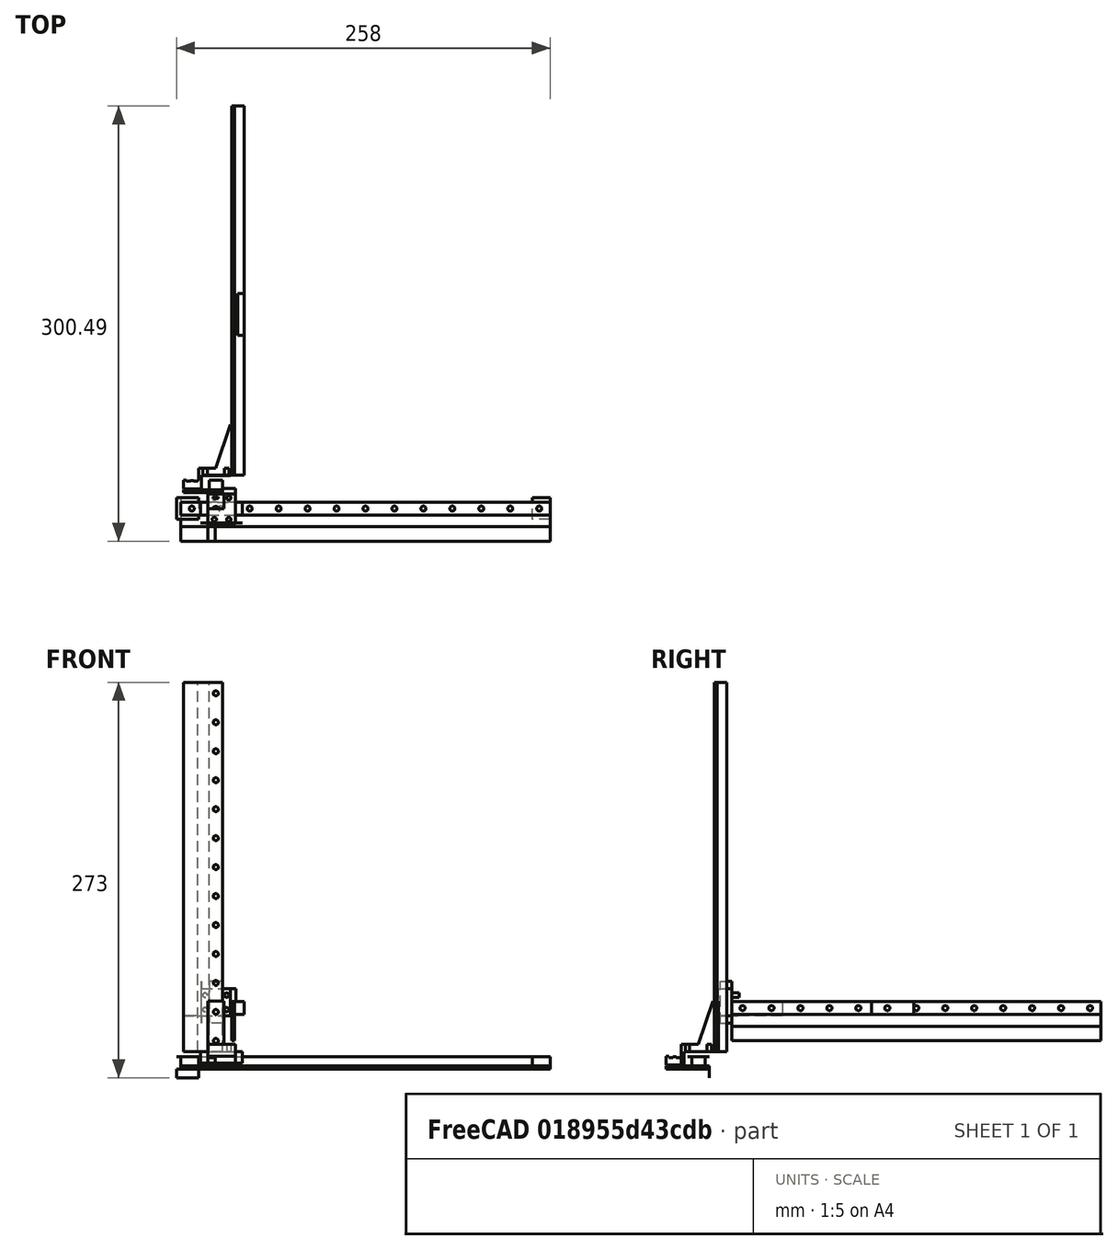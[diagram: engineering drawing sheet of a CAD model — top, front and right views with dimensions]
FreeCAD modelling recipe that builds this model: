
FCSTD DOCUMENT  (FreeCAD 0.21R33668 +26 (Git))
Label: v7
License: All rights reserved
LicenseURL: http://en.wikipedia.org/wiki/All_rights_reserved
objects: App::FeaturePython×94, Part::FeaturePython×66, App::Link×14
note: 65 computed .brp shape members not serialized (recipe doc carries the construction recipe); baked Part::Feature solids carry a one-line shape summary decoded from their .brp
EXTERNAL_REF file=parts/Base.FCStd obj=Body
EXTERNAL_REF file=parts/PCB_Linear_Potentiometer.FCStd obj=Body
EXTERNAL_REF file=parts/MG/mgn9c_13.FCStd obj=Body
EXTERNAL_REF file=parts/MG/mgn9c_slide.FCStd obj=Body001
EXTERNAL_REF file=parts/NormalConnector.FCStd obj=Body
EXTERNAL_REF file=parts/Joystick_Holder.FCStd obj=Body

FEATURE [App::Link] Link  label="Base_PCBLB"
  LinkedObject = -> <external parts/Base.FCStd>#Body
  _LinkOwner = 433
FEATURE [App::Link] Link001  label="PCB"
  LinkPlacement = pos=(-2.497e-13,7.45963e-11,-2) rot=(0,0,1;0rad)
  LinkedObject = -> <external parts/PCB_Linear_Potentiometer.FCStd>#Body
  Placement = pos=(-2.497e-13,7.45963e-11,-2) rot=(0,0,1;0rad)
  _LinkOwner = 433
FEATURE [App::Link] Link002  label="RailXL"
  LinkPlacement = pos=(1.4e-15,8e-16,-3.48e-14) rot=(0,0,1;0rad)
  LinkedObject = -> <external parts/MG/mgn9c_13.FCStd>#Body
  Placement = pos=(1.4e-15,8e-16,-3.48e-14) rot=(0,0,1;0rad)
  _LinkOwner = 433
FEATURE [App::Link] Link003  label="Base_PCB"
  LinkPlacement = pos=(255,9,-4.15529e-11) rot=(0,0,1;3.14159rad)
  LinkedObject = -> <external parts/Base.FCStd>#Body
  Placement = pos=(255,9,-4.15529e-11) rot=(0,0,1;3.14159rad)
  _LinkOwner = 433
FEATURE [App::Link] Link004  label="Slide"
  LinkPlacement = pos=(13.624,-5.5,2) rot=(0,0,1;0rad)
  LinkedObject = -> <external parts/MG/mgn9c_slide.FCStd>#Body001
  Placement = pos=(13.624,-5.5,2) rot=(0,0,1;0rad)
  _LinkOwner = 433
FEATURE [App::Link] Link005  label="NormalConnector"
  LinkPlacement = pos=(18.624,-5.5,4.00003) rot=(0,0,1;0rad)
  LinkedObject = -> <external parts/NormalConnector.FCStd>#Body
  Placement = pos=(18.624,-5.5,4.00003) rot=(0,0,1;0rad)
  _LinkOwner = 433
FEATURE [App::Link] Link006  label="PCB001"
  LinkPlacement = pos=(19.624,15.5,10) rot=(0.57735,0.57735,0.57735;4.18879rad)
  LinkedObject = -> <external parts/PCB_Linear_Potentiometer.FCStd>#Body
  Placement = pos=(19.624,15.5,10) rot=(0.57735,0.57735,0.57735;4.18879rad)
  _LinkOwner = 433
FEATURE [App::Link] Link007  label="Rail"
  LinkPlacement = pos=(19.624,17.5,10) rot=(0.57735,0.57735,0.57735;4.18879rad)
  LinkedObject = -> <external parts/MG/mgn9c_13.FCStd>#Body
  Placement = pos=(19.624,17.5,10) rot=(0.57735,0.57735,0.57735;4.18879rad)
  _LinkOwner = 433
FEATURE [App::Link] Link008  label="Slide001"
  LinkPlacement = pos=(34.124,19.5,58.4856) rot=(-0.57735,0.57735,0.57735;2.0944rad)
  LinkedObject = -> <external parts/MG/mgn9c_slide.FCStd>#Body001
  Placement = pos=(34.124,19.5,58.4856) rot=(-0.57735,0.57735,0.57735;2.0944rad)
  _LinkOwner = 433
FEATURE [App::Link] Link009  label="NormalConnector001"
  LinkPlacement = pos=(14.124,21.5,34.5856) rot=(0.57735,0.57735,0.57735;4.18879rad)
  LinkedObject = -> <external parts/NormalConnector.FCStd>#Body
  Placement = pos=(14.124,21.5,34.5856) rot=(0.57735,0.57735,0.57735;4.18879rad)
  _LinkOwner = 433
FEATURE [App::Link] Link010  label="Rail001"
  LinkPlacement = pos=(37.124,27.5,35.5856) rot=(0.57735,0.57735,0.57735;2.0944rad)
  LinkedObject = -> <external parts/MG/mgn9c_13.FCStd>#Body
  Placement = pos=(37.124,27.5,35.5856) rot=(0.57735,0.57735,0.57735;2.0944rad)
  _LinkOwner = 433
FEATURE [App::Link] Link011  label="PCB002"
  LinkPlacement = pos=(35.124,27.5,35.5856) rot=(0.57735,0.57735,0.57735;2.0944rad)
  LinkedObject = -> <external parts/PCB_Linear_Potentiometer.FCStd>#Body
  Placement = pos=(35.124,27.5,35.5856) rot=(0.57735,0.57735,0.57735;2.0944rad)
  _LinkOwner = 433
FEATURE [App::Link] Link012  label="Slide002"
  LinkPlacement = pos=(39.124,153.145,50.0856) rot=(0.57735,-0.57735,0.57735;4.18879rad)
  LinkedObject = -> <external parts/MG/mgn9c_slide.FCStd>#Body001
  Placement = pos=(39.124,153.145,50.0856) rot=(0.57735,-0.57735,0.57735;4.18879rad)
  _LinkOwner = 433
FEATURE [App::Link] Link013  label="JoystickHolder"
  LinkPlacement = pos=(171.029,100,-4) rot=(0,0,1;3.14159rad)
  LinkedObject = -> <external parts/Joystick_Holder.FCStd>#Body
  Placement = pos=(171.029,100,-4) rot=(0,0,1;3.14159rad)
  _LinkOwner = 433
FEATURE [Part::FeaturePython] Parts  # WARN: FeaturePython — macro-defined, semantics opaque (R4)
  Group = -> [Link,Link001,Link002,Link003,Link004,Link005,Link006,Link007,Link008,Link009,Link010,Link011,Link012,Link013]
  GroupMode = 0
FEATURE [Part::FeaturePython] Assembly  # WARN: FeaturePython — macro-defined, semantics opaque (R4)
  AutoRelax = true
  BuildShape = 0
  Freeze = false
  Group = -> [Constraints,Elements,Parts]
  Verbose = false
  _SolverType = 1
  _Version = 1
FEATURE [App::FeaturePython] Constraints  # WARN: FeaturePython — macro-defined, semantics opaque (R4)
  Group = -> [Constraint,Constraint001,Constraint003,Constraint004,Constraint005,Constraint006,Constraint007,Constraint008,Constraint009,Constraint010,Constraint011,Constraint012,Constraint019,Constraint020,Constraint021,Constraint022,Constraint023,Constraint025,Constraint026,Constraint027,Constraint029,Constraint030,Constraint031,Constraint035,Constraint037,Constraint038,Constraint039,Constraint040,+3 more]
  _Version = 1
FEATURE [App::FeaturePython] Elements  # WARN: FeaturePython — macro-defined, semantics opaque (R4)
  Group = -> [_Element,_Element001,_Element002,_Element003,_Element004,_Element005,_Element006,_Element007,_Element008,_Element009,_Element010,_Element011,_Element012,_Element013,_Element014,_Element015,_Element016,_Element017,_Element018,_Element019,_Element020,_Element021,_Element022,_Element023,_Element024,_Element025,_Element026,_Element027,_Element028,_Element029,_Element030,_Element031,_Element032,+31 more]
FEATURE [App::FeaturePython] Constraint  label="Locked"  # WARN: FeaturePython — macro-defined, semantics opaque (R4)
  Disabled = false
  Group = -> [ElementLink]
  _ConstraintType = 0
  _Parent = -> Constraints
FEATURE [App::FeaturePython] ElementLink  label="_Element"  # link proxy (typed FeaturePython)
  LinkTransform = true
  LinkedObject = -> _Element
  _Parent = -> Constraint
FEATURE [Part::FeaturePython] _Element  # link proxy (typed FeaturePython)
  Detach = false
  LinkTransform = true
  LinkedObject = -> Link [Pocket.Face5]
  _Parent = -> Elements
FEATURE [App::FeaturePython] Constraint001  label="PlaneAlignment"  # WARN: FeaturePython — macro-defined, semantics opaque (R4)
  Angle = 0
  AnglePitch = 0
  AngleRoll = 0
  Cascade = false
  Disabled = false
  Group = -> [ElementLink001,ElementLink002]
  LockAngle = false
  _ConstraintType = 37
  _Parent = -> Constraints
FEATURE [App::FeaturePython] ElementLink001  label="_Element001"  # link proxy (typed FeaturePython)
  LinkTransform = true
  LinkedObject = -> _Element001
  _Parent = -> Constraint001
FEATURE [Part::FeaturePython] _Element001  # link proxy (typed FeaturePython)
  Detach = false
  LinkTransform = true
  LinkedObject = -> Link001 [Pad001.Face4]
  _Parent = -> Elements
FEATURE [App::FeaturePython] ElementLink002  label="_Element002"  # link proxy (typed FeaturePython)
  LinkTransform = true
  LinkedObject = -> _Element002
  _Parent = -> Constraint001
FEATURE [Part::FeaturePython] _Element002  # link proxy (typed FeaturePython)
  Detach = false
  LinkTransform = true
  LinkedObject = -> Link [Pocket.Face11]
  _Parent = -> Elements
FEATURE [Part::FeaturePython] _Element003  # link proxy (typed FeaturePython)
  Detach = false
  LinkTransform = true
  LinkedObject = -> Link [Pocket.Face18]
  _Parent = -> Elements
FEATURE [Part::FeaturePython] _Element004  # link proxy (typed FeaturePython)
  Detach = false
  LinkTransform = true
  LinkedObject = -> Link001 [Pad001.Face1]
  _Parent = -> Elements
FEATURE [App::FeaturePython] Constraint003  label="PlaneAlignment002"  # WARN: FeaturePython — macro-defined, semantics opaque (R4)
  Angle = 0
  AnglePitch = 0
  AngleRoll = 0
  Cascade = false
  Disabled = false
  Group = -> [ElementLink005,ElementLink006]
  LockAngle = false
  _ConstraintType = 37
  _Parent = -> Constraints
FEATURE [App::FeaturePython] ElementLink005  label="_Element005"  # link proxy (typed FeaturePython)
  LinkTransform = true
  LinkedObject = -> _Element005
  _Parent = -> Constraint003
FEATURE [Part::FeaturePython] _Element005  # link proxy (typed FeaturePython)
  Detach = false
  LinkTransform = true
  LinkedObject = -> Link001 [Pad001.Face2]
  _Parent = -> Elements
FEATURE [App::FeaturePython] ElementLink006  label="_Element006"  # link proxy (typed FeaturePython)
  LinkTransform = true
  LinkedObject = -> _Element006
  _Parent = -> Constraint003
FEATURE [Part::FeaturePython] _Element006  # link proxy (typed FeaturePython)
  Detach = false
  LinkTransform = true
  LinkedObject = -> Link [Pocket.Face4]
  _Parent = -> Elements
FEATURE [App::FeaturePython] Constraint004  label="PlaneAlignment003"  # WARN: FeaturePython — macro-defined, semantics opaque (R4)
  Angle = 0
  AnglePitch = 0
  AngleRoll = 0
  Cascade = false
  Disabled = false
  Group = -> [ElementLink007,ElementLink008]
  LockAngle = false
  _ConstraintType = 37
  _Parent = -> Constraints
FEATURE [App::FeaturePython] ElementLink007  label="_Element007"  # link proxy (typed FeaturePython)
  LinkTransform = true
  LinkedObject = -> _Element007
  _Parent = -> Constraint004
FEATURE [Part::FeaturePython] _Element007  # link proxy (typed FeaturePython)
  Detach = false
  LinkTransform = true
  LinkedObject = -> Link [Pocket.Face1]
  _Parent = -> Elements
FEATURE [App::FeaturePython] ElementLink008  label="_Element008"  # link proxy (typed FeaturePython)
  LinkTransform = true
  LinkedObject = -> _Element008
  _Parent = -> Constraint004
FEATURE [Part::FeaturePython] _Element008  # link proxy (typed FeaturePython)
  Detach = false
  LinkTransform = true
  LinkedObject = -> Link002 [LinearPattern.Face2]
  _Parent = -> Elements
FEATURE [App::FeaturePython] Constraint005  label="PlaneAlignment004"  # WARN: FeaturePython — macro-defined, semantics opaque (R4)
  Angle = 0
  AnglePitch = 0
  AngleRoll = 0
  Cascade = false
  Disabled = false
  Group = -> [ElementLink009,ElementLink010]
  LockAngle = false
  _ConstraintType = 37
  _Parent = -> Constraints
FEATURE [App::FeaturePython] ElementLink009  label="_Element009"  # link proxy (typed FeaturePython)
  LinkTransform = true
  LinkedObject = -> _Element009
  _Parent = -> Constraint005
FEATURE [Part::FeaturePython] _Element009  # link proxy (typed FeaturePython)
  Detach = false
  LinkTransform = true
  LinkedObject = -> Link002 [LinearPattern.Face6]
  _Parent = -> Elements
FEATURE [App::FeaturePython] ElementLink010  label="_Element010"  # link proxy (typed FeaturePython)
  LinkTransform = true
  LinkedObject = -> _Element010
  _Parent = -> Constraint005
FEATURE [Part::FeaturePython] _Element010  # link proxy (typed FeaturePython)
  Detach = false
  LinkTransform = true
  LinkedObject = -> Link [Pocket.Face3]
  _Parent = -> Elements
FEATURE [App::FeaturePython] Constraint006  label="PlaneAlignment005"  # WARN: FeaturePython — macro-defined, semantics opaque (R4)
  Angle = 0
  AnglePitch = 0
  AngleRoll = 0
  Cascade = false
  Disabled = false
  Group = -> [ElementLink011,ElementLink012]
  LockAngle = false
  _ConstraintType = 37
  _Parent = -> Constraints
FEATURE [App::FeaturePython] ElementLink011  label="_Element011"  # link proxy (typed FeaturePython)
  LinkTransform = true
  LinkedObject = -> _Element011
  _Parent = -> Constraint006
FEATURE [Part::FeaturePython] _Element011  # link proxy (typed FeaturePython)
  Detach = false
  LinkTransform = true
  LinkedObject = -> Link002 [LinearPattern.Face4]
  _Parent = -> Elements
FEATURE [App::FeaturePython] ElementLink012  label="_Element012"  # link proxy (typed FeaturePython)
  LinkTransform = true
  LinkedObject = -> _Element012
  _Parent = -> Constraint006
FEATURE [Part::FeaturePython] _Element012  # link proxy (typed FeaturePython)
  Detach = false
  LinkTransform = true
  LinkedObject = -> Link001 [Pad001.Face5]
  _Parent = -> Elements
FEATURE [App::FeaturePython] Constraint007  label="PlaneAlignment006"  # WARN: FeaturePython — macro-defined, semantics opaque (R4)
  Angle = 0
  AnglePitch = 0
  AngleRoll = 0
  Cascade = false
  Disabled = false
  Group = -> [ElementLink013,ElementLink014]
  LockAngle = false
  _ConstraintType = 37
  _Parent = -> Constraints
FEATURE [App::FeaturePython] ElementLink013  label="_Element004"  # link proxy (typed FeaturePython)
  LinkTransform = true
  LinkedObject = -> _Element004
  _Parent = -> Constraint007
FEATURE [App::FeaturePython] ElementLink014  label="_Element009"  # link proxy (typed FeaturePython)
  LinkTransform = true
  LinkedObject = -> _Element009
  _Parent = -> Constraint007
FEATURE [App::FeaturePython] Constraint008  label="PlaneAlignment007"  # WARN: FeaturePython — macro-defined, semantics opaque (R4)
  Angle = 0
  AnglePitch = 0
  AngleRoll = 0
  Cascade = false
  Disabled = false
  Group = -> [ElementLink015,ElementLink016]
  LockAngle = false
  _ConstraintType = 37
  _Parent = -> Constraints
FEATURE [App::FeaturePython] ElementLink015  label="_Element013"  # link proxy (typed FeaturePython)
  LinkTransform = true
  LinkedObject = -> _Element013
  _Parent = -> Constraint008
FEATURE [Part::FeaturePython] _Element013  # link proxy (typed FeaturePython)
  Detach = false
  LinkTransform = true
  LinkedObject = -> Link003 [Pocket.Face2]
  _Parent = -> Elements
FEATURE [App::FeaturePython] ElementLink016  label="_Element009"  # link proxy (typed FeaturePython)
  LinkTransform = true
  LinkedObject = -> _Element009
  _Parent = -> Constraint008
FEATURE [App::FeaturePython] Constraint009  label="PlaneAlignment008"  # WARN: FeaturePython — macro-defined, semantics opaque (R4)
  Angle = 0
  AnglePitch = 0
  AngleRoll = 0
  Cascade = false
  Disabled = false
  Group = -> [ElementLink017,ElementLink018]
  LockAngle = false
  _ConstraintType = 37
  _Parent = -> Constraints
FEATURE [App::FeaturePython] ElementLink017  label="_Element014"  # link proxy (typed FeaturePython)
  LinkTransform = true
  LinkedObject = -> _Element014
  _Parent = -> Constraint009
FEATURE [Part::FeaturePython] _Element014  # link proxy (typed FeaturePython)
  Detach = false
  LinkTransform = true
  LinkedObject = -> Link003 [Pocket.Face11]
  _Parent = -> Elements
FEATURE [App::FeaturePython] ElementLink018  label="_Element001"  # link proxy (typed FeaturePython)
  LinkTransform = true
  LinkedObject = -> _Element001
  _Parent = -> Constraint009
FEATURE [App::FeaturePython] Constraint010  label="PlaneAlignment009"  # WARN: FeaturePython — macro-defined, semantics opaque (R4)
  Angle = 0
  AnglePitch = 0
  AngleRoll = 0
  Cascade = false
  Disabled = false
  Group = -> [ElementLink019,ElementLink020]
  LockAngle = false
  _ConstraintType = 37
  _Parent = -> Constraints
FEATURE [App::FeaturePython] ElementLink019  label="_Element015"  # link proxy (typed FeaturePython)
  LinkTransform = true
  LinkedObject = -> _Element015
  _Parent = -> Constraint010
FEATURE [Part::FeaturePython] _Element015  # link proxy (typed FeaturePython)
  Detach = false
  LinkTransform = true
  LinkedObject = -> Link003 [Pocket.Face1]
  _Parent = -> Elements
FEATURE [App::FeaturePython] ElementLink020  label="_Element016"  # link proxy (typed FeaturePython)
  LinkTransform = true
  LinkedObject = -> _Element016
  _Parent = -> Constraint010
FEATURE [Part::FeaturePython] _Element016  # link proxy (typed FeaturePython)
  Detach = false
  LinkTransform = true
  LinkedObject = -> Link002 [LinearPattern.Face3]
  _Parent = -> Elements
FEATURE [App::FeaturePython] Constraint011  label="PlaneAlignment010"  # WARN: FeaturePython — macro-defined, semantics opaque (R4)
  Angle = 0
  AnglePitch = 0
  AngleRoll = 0
  Cascade = false
  Disabled = false
  Group = -> [ElementLink021,ElementLink022]
  LockAngle = false
  _ConstraintType = 37
  _Parent = -> Constraints
FEATURE [App::FeaturePython] ElementLink021  label="_Element017"  # link proxy (typed FeaturePython)
  LinkTransform = true
  LinkedObject = -> _Element017
  _Parent = -> Constraint011
FEATURE [Part::FeaturePython] _Element017  # link proxy (typed FeaturePython)
  Detach = false
  LinkTransform = true
  LinkedObject = -> Link004 [Pocket003.Face12]
  _Parent = -> Elements
FEATURE [App::FeaturePython] ElementLink022  label="_Element009"  # link proxy (typed FeaturePython)
  LinkTransform = true
  LinkedObject = -> _Element009
  _Parent = -> Constraint011
FEATURE [App::FeaturePython] Constraint012  label="PlaneAlignment011"  # WARN: FeaturePython — macro-defined, semantics opaque (R4)
  Angle = 0
  AnglePitch = 0
  AngleRoll = 0
  Cascade = false
  Disabled = false
  Group = -> [ElementLink023,ElementLink024]
  LockAngle = false
  _ConstraintType = 37
  _Parent = -> Constraints
FEATURE [App::FeaturePython] ElementLink023  label="_Element018"  # link proxy (typed FeaturePython)
  LinkTransform = true
  LinkedObject = -> _Element018
  _Parent = -> Constraint012
FEATURE [Part::FeaturePython] _Element018  # link proxy (typed FeaturePython)
  Detach = false
  LinkTransform = true
  LinkedObject = -> Link004 [Pocket003.Face11]
  _Parent = -> Elements
FEATURE [App::FeaturePython] ElementLink024  label="_Element019"  # link proxy (typed FeaturePython)
  LinkTransform = true
  LinkedObject = -> _Element019
  _Parent = -> Constraint012
FEATURE [Part::FeaturePython] _Element019  # link proxy (typed FeaturePython)
  Detach = false
  LinkTransform = true
  LinkedObject = -> Link002 [LinearPattern.Face5]
  _Parent = -> Elements
FEATURE [Part::FeaturePython] _Element020  # link proxy (typed FeaturePython)
  Detach = false
  LinkTransform = true
  LinkedObject = -> Link005 [Pocket006.Face5]
  _Parent = -> Elements
FEATURE [Part::FeaturePython] _Element021  # link proxy (typed FeaturePython)
  Detach = false
  LinkTransform = true
  LinkedObject = -> Link004 [Pocket003.Face5]
  _Parent = -> Elements
FEATURE [Part::FeaturePython] _Element022  # link proxy (typed FeaturePython)
  Detach = false
  LinkTransform = true
  LinkedObject = -> Link005 [Pocket006.Face2]
  _Parent = -> Elements
FEATURE [Part::FeaturePython] _Element023  # link proxy (typed FeaturePython)
  Detach = false
  LinkTransform = true
  LinkedObject = -> Link004 [Pocket003.Face6]
  _Parent = -> Elements
FEATURE [Part::FeaturePython] _Element024  # link proxy (typed FeaturePython)
  Detach = false
  LinkTransform = true
  LinkedObject = -> Link005 [Pocket006.Face1]
  _Parent = -> Elements
FEATURE [Part::FeaturePython] _Element025  # link proxy (typed FeaturePython)
  Detach = false
  LinkTransform = true
  LinkedObject = -> Link004 [Pocket003.Face1]
  _Parent = -> Elements
FEATURE [Part::FeaturePython] _Element026  # link proxy (typed FeaturePython)
  Detach = false
  LinkTransform = true
  LinkedObject = -> Link006 [Pad001.Face1]
  _Parent = -> Elements
FEATURE [Part::FeaturePython] _Element027  # link proxy (typed FeaturePython)
  Detach = false
  LinkTransform = true
  LinkedObject = -> Link005 [Pocket006.Face9]
  _Parent = -> Elements
FEATURE [Part::FeaturePython] _Element028  # link proxy (typed FeaturePython)
  Detach = false
  LinkTransform = true
  LinkedObject = -> Link006 [Pad001.Face4]
  _Parent = -> Elements
FEATURE [Part::FeaturePython] _Element029  # link proxy (typed FeaturePython)
  Detach = false
  LinkTransform = true
  LinkedObject = -> Link005 [Pocket006.Face7]
  _Parent = -> Elements
FEATURE [Part::FeaturePython] _Element030  # link proxy (typed FeaturePython)
  Detach = false
  LinkTransform = true
  LinkedObject = -> Link006 [Pad001.Face2]
  _Parent = -> Elements
FEATURE [App::FeaturePython] Constraint019  label="PlaneAlignment018"  # WARN: FeaturePython — macro-defined, semantics opaque (R4)
  Angle = 0
  AnglePitch = 0
  AngleRoll = 0
  Cascade = false
  Disabled = false
  Group = -> [ElementLink037,ElementLink038]
  LockAngle = false
  _ConstraintType = 37
  _Parent = -> Constraints
FEATURE [App::FeaturePython] ElementLink037  label="_Element031"  # link proxy (typed FeaturePython)
  LinkTransform = true
  LinkedObject = -> _Element031
  _Parent = -> Constraint019
FEATURE [Part::FeaturePython] _Element031  # link proxy (typed FeaturePython)
  Detach = false
  LinkTransform = true
  LinkedObject = -> Link007 [LinearPattern.Face6]
  _Parent = -> Elements
FEATURE [App::FeaturePython] ElementLink038  label="_Element026"  # link proxy (typed FeaturePython)
  LinkTransform = true
  LinkedObject = -> _Element026
  _Parent = -> Constraint019
FEATURE [App::FeaturePython] Constraint020  label="PlaneAlignment019"  # WARN: FeaturePython — macro-defined, semantics opaque (R4)
  Angle = 0
  AnglePitch = 0
  AngleRoll = 0
  Cascade = false
  Disabled = false
  Group = -> [ElementLink039,ElementLink040]
  LockAngle = false
  _ConstraintType = 37
  _Parent = -> Constraints
FEATURE [App::FeaturePython] ElementLink039  label="_Element032"  # link proxy (typed FeaturePython)
  LinkTransform = true
  LinkedObject = -> _Element032
  _Parent = -> Constraint020
FEATURE [Part::FeaturePython] _Element032  # link proxy (typed FeaturePython)
  Detach = false
  LinkTransform = true
  LinkedObject = -> Link007 [LinearPattern.Face2]
  _Parent = -> Elements
FEATURE [App::FeaturePython] ElementLink040  label="_Element030"  # link proxy (typed FeaturePython)
  LinkTransform = true
  LinkedObject = -> _Element030
  _Parent = -> Constraint020
FEATURE [App::FeaturePython] Constraint021  label="PlaneAlignment020"  # WARN: FeaturePython — macro-defined, semantics opaque (R4)
  Angle = 0
  AnglePitch = 0
  AngleRoll = 0
  Cascade = false
  Disabled = false
  Group = -> [ElementLink041,ElementLink042]
  LockAngle = false
  _ConstraintType = 37
  _Parent = -> Constraints
FEATURE [App::FeaturePython] ElementLink041  label="_Element033"  # link proxy (typed FeaturePython)
  LinkTransform = true
  LinkedObject = -> _Element033
  _Parent = -> Constraint021
FEATURE [Part::FeaturePython] _Element033  # link proxy (typed FeaturePython)
  Detach = false
  LinkTransform = true
  LinkedObject = -> Link007 [LinearPattern.Face4]
  _Parent = -> Elements
FEATURE [App::FeaturePython] ElementLink042  label="_Element034"  # link proxy (typed FeaturePython)
  LinkTransform = true
  LinkedObject = -> _Element034
  _Parent = -> Constraint021
FEATURE [Part::FeaturePython] _Element034  # link proxy (typed FeaturePython)
  Detach = false
  LinkTransform = true
  LinkedObject = -> Link006 [Pad001.Face5]
  _Parent = -> Elements
FEATURE [App::FeaturePython] Constraint022  label="PlaneAlignment021"  # WARN: FeaturePython — macro-defined, semantics opaque (R4)
  Angle = 0
  AnglePitch = 0
  AngleRoll = 0
  Cascade = false
  Disabled = false
  Group = -> [ElementLink043,ElementLink044]
  LockAngle = false
  _ConstraintType = 37
  _Parent = -> Constraints
FEATURE [App::FeaturePython] ElementLink043  label="_Element035"  # link proxy (typed FeaturePython)
  LinkTransform = true
  LinkedObject = -> _Element035
  _Parent = -> Constraint022
FEATURE [Part::FeaturePython] _Element035  # link proxy (typed FeaturePython)
  Detach = false
  LinkTransform = true
  LinkedObject = -> Link008 [Pocket003.Face12]
  _Parent = -> Elements
FEATURE [App::FeaturePython] ElementLink044  label="_Element036"  # link proxy (typed FeaturePython)
  LinkTransform = true
  LinkedObject = -> _Element036
  _Parent = -> Constraint022
FEATURE [Part::FeaturePython] _Element036  # link proxy (typed FeaturePython)
  Detach = false
  LinkTransform = true
  LinkedObject = -> Link007 [LinearPattern.Face1]
  _Parent = -> Elements
FEATURE [App::FeaturePython] Constraint023  label="PlaneAlignment022"  # WARN: FeaturePython — macro-defined, semantics opaque (R4)
  Angle = 0
  AnglePitch = 0
  AngleRoll = 0
  Cascade = false
  Disabled = false
  Group = -> [ElementLink045,ElementLink046]
  LockAngle = false
  _ConstraintType = 37
  _Parent = -> Constraints
FEATURE [App::FeaturePython] ElementLink045  label="_Element037"  # link proxy (typed FeaturePython)
  LinkTransform = true
  LinkedObject = -> _Element037
  _Parent = -> Constraint023
FEATURE [Part::FeaturePython] _Element037  # link proxy (typed FeaturePython)
  Detach = false
  LinkTransform = true
  LinkedObject = -> Link008 [Pocket003.Face11]
  _Parent = -> Elements
FEATURE [App::FeaturePython] ElementLink046  label="_Element038"  # link proxy (typed FeaturePython)
  LinkTransform = true
  LinkedObject = -> _Element038
  _Parent = -> Constraint023
FEATURE [Part::FeaturePython] _Element038  # link proxy (typed FeaturePython)
  Detach = false
  LinkTransform = true
  LinkedObject = -> Link007 [LinearPattern.Face5]
  _Parent = -> Elements
FEATURE [Part::FeaturePython] _Element039  # link proxy (typed FeaturePython)
  Detach = false
  LinkTransform = true
  LinkedObject = -> Link005 [Pocket006.Face34]
  _Parent = -> Elements
FEATURE [App::FeaturePython] Constraint025  label="PlaneAlignment024"  # WARN: FeaturePython — macro-defined, semantics opaque (R4)
  Angle = 0
  AnglePitch = 0
  AngleRoll = 0
  Cascade = false
  Disabled = false
  Group = -> [ElementLink049,ElementLink050]
  LockAngle = false
  _ConstraintType = 37
  _Parent = -> Constraints
FEATURE [App::FeaturePython] ElementLink049  label="_Element030"  # link proxy (typed FeaturePython)
  LinkTransform = true
  LinkedObject = -> _Element030
  _Parent = -> Constraint025
FEATURE [App::FeaturePython] ElementLink050  label="_Element040"  # link proxy (typed FeaturePython)
  LinkTransform = true
  LinkedObject = -> _Element040
  _Parent = -> Constraint025
FEATURE [Part::FeaturePython] _Element040  # link proxy (typed FeaturePython)
  Detach = false
  LinkTransform = true
  LinkedObject = -> Link005 [Pocket006.Face12]
  _Parent = -> Elements
FEATURE [App::FeaturePython] Constraint026  label="PlaneAlignment025"  # WARN: FeaturePython — macro-defined, semantics opaque (R4)
  Angle = 0
  AnglePitch = 0
  AngleRoll = 0
  Cascade = false
  Disabled = false
  Group = -> [ElementLink051,ElementLink052]
  LockAngle = false
  _ConstraintType = 37
  _Parent = -> Constraints
FEATURE [App::FeaturePython] ElementLink051  label="_Element022"  # link proxy (typed FeaturePython)
  LinkTransform = true
  LinkedObject = -> _Element022
  _Parent = -> Constraint026
FEATURE [App::FeaturePython] ElementLink052  label="_Element041"  # link proxy (typed FeaturePython)
  LinkTransform = true
  LinkedObject = -> _Element041
  _Parent = -> Constraint026
FEATURE [Part::FeaturePython] _Element041  # link proxy (typed FeaturePython)
  Detach = false
  LinkTransform = true
  LinkedObject = -> Link004 [Pocket003.Face7]
  _Parent = -> Elements
FEATURE [App::FeaturePython] Constraint027  label="PlaneAlignment026"  # WARN: FeaturePython — macro-defined, semantics opaque (R4)
  Angle = 0
  AnglePitch = 0
  AngleRoll = 0
  Cascade = false
  Disabled = false
  Group = -> [ElementLink053,ElementLink054]
  LockAngle = false
  _ConstraintType = 37
  _Parent = -> Constraints
FEATURE [App::FeaturePython] ElementLink053  label="_Element042"  # link proxy (typed FeaturePython)
  LinkTransform = true
  LinkedObject = -> _Element042
  _Parent = -> Constraint027
FEATURE [Part::FeaturePython] _Element042  # link proxy (typed FeaturePython)
  Detach = false
  LinkTransform = true
  LinkedObject = -> Link005 [Pocket006.Face13]
  _Parent = -> Elements
FEATURE [App::FeaturePython] ElementLink054  label="_Element025"  # link proxy (typed FeaturePython)
  LinkTransform = true
  LinkedObject = -> _Element025
  _Parent = -> Constraint027
FEATURE [Part::FeaturePython] _Element043  # link proxy (typed FeaturePython)
  Detach = false
  LinkTransform = true
  LinkedObject = -> Link005 [Pocket006.Face35]
  _Parent = -> Elements
FEATURE [App::FeaturePython] Constraint029  label="PlaneAlignment028"  # WARN: FeaturePython — macro-defined, semantics opaque (R4)
  Angle = 0
  AnglePitch = 0
  AngleRoll = 0
  Cascade = false
  Disabled = false
  Group = -> [ElementLink057,ElementLink058]
  LockAngle = false
  _ConstraintType = 37
  _Parent = -> Constraints
FEATURE [App::FeaturePython] ElementLink057  label="_Element044"  # link proxy (typed FeaturePython)
  LinkTransform = true
  LinkedObject = -> _Element044
  _Parent = -> Constraint029
FEATURE [Part::FeaturePython] _Element044  # link proxy (typed FeaturePython)
  Detach = false
  LinkTransform = true
  LinkedObject = -> Link009 [Pocket006.Face13]
  _Parent = -> Elements
FEATURE [App::FeaturePython] ElementLink058  label="_Element045"  # link proxy (typed FeaturePython)
  LinkTransform = true
  LinkedObject = -> _Element045
  _Parent = -> Constraint029
FEATURE [Part::FeaturePython] _Element045  # link proxy (typed FeaturePython)
  Detach = false
  LinkTransform = true
  LinkedObject = -> Link008 [Pocket003.Face14]
  _Parent = -> Elements
FEATURE [App::FeaturePython] Constraint030  label="PlaneAlignment029"  # WARN: FeaturePython — macro-defined, semantics opaque (R4)
  Angle = 0
  AnglePitch = 0
  AngleRoll = 0
  Cascade = false
  Disabled = false
  Group = -> [ElementLink059,ElementLink060]
  LockAngle = false
  _ConstraintType = 37
  _Parent = -> Constraints
FEATURE [App::FeaturePython] ElementLink059  label="_Element046"  # link proxy (typed FeaturePython)
  LinkTransform = true
  LinkedObject = -> _Element046
  _Parent = -> Constraint030
FEATURE [Part::FeaturePython] _Element046  # link proxy (typed FeaturePython)
  Detach = false
  LinkTransform = true
  LinkedObject = -> Link009 [Pocket006.Face2]
  _Parent = -> Elements
FEATURE [App::FeaturePython] ElementLink060  label="_Element047"  # link proxy (typed FeaturePython)
  LinkTransform = true
  LinkedObject = -> _Element047
  _Parent = -> Constraint030
FEATURE [Part::FeaturePython] _Element047  # link proxy (typed FeaturePython)
  Detach = false
  LinkTransform = true
  LinkedObject = -> Link008 [Pocket003.Face5]
  _Parent = -> Elements
FEATURE [App::FeaturePython] Constraint031  label="PlaneAlignment030"  # WARN: FeaturePython — macro-defined, semantics opaque (R4)
  Angle = 0
  AnglePitch = 0
  AngleRoll = 0
  Cascade = false
  Disabled = false
  Group = -> [ElementLink061,ElementLink062]
  LockAngle = false
  _ConstraintType = 37
  _Parent = -> Constraints
FEATURE [App::FeaturePython] ElementLink061  label="_Element048"  # link proxy (typed FeaturePython)
  LinkTransform = true
  LinkedObject = -> _Element048
  _Parent = -> Constraint031
FEATURE [Part::FeaturePython] _Element048  # link proxy (typed FeaturePython)
  Detach = false
  LinkTransform = true
  LinkedObject = -> Link009 [Pocket006.Face12]
  _Parent = -> Elements
FEATURE [App::FeaturePython] ElementLink062  label="_Element049"  # link proxy (typed FeaturePython)
  LinkTransform = true
  LinkedObject = -> _Element049
  _Parent = -> Constraint031
FEATURE [Part::FeaturePython] _Element049  # link proxy (typed FeaturePython)
  Detach = false
  LinkTransform = true
  LinkedObject = -> Link008 [Pocket003.Face6]
  _Parent = -> Elements
FEATURE [Part::FeaturePython] _Element050  # link proxy (typed FeaturePython)
  Detach = false
  LinkTransform = true
  LinkedObject = -> Link010 [LinearPattern.Face6]
  _Parent = -> Elements
FEATURE [Part::FeaturePython] _Element051  # link proxy (typed FeaturePython)
  Detach = false
  LinkTransform = true
  LinkedObject = -> Link009 [Pocket006.Face34]
  _Parent = -> Elements
FEATURE [Part::FeaturePython] _Element052  # link proxy (typed FeaturePython)
  Detach = false
  LinkTransform = true
  LinkedObject = -> Link010 [LinearPattern.Face2]
  _Parent = -> Elements
FEATURE [Part::FeaturePython] _Element053  # link proxy (typed FeaturePython)
  Detach = false
  LinkTransform = true
  LinkedObject = -> Link011 [Pad001.Face1]
  _Parent = -> Elements
FEATURE [App::FeaturePython] Constraint035  label="PlaneAlignment034"  # WARN: FeaturePython — macro-defined, semantics opaque (R4)
  Angle = 0
  AnglePitch = 0
  AngleRoll = 0
  Cascade = false
  Disabled = false
  Group = -> [ElementLink069,ElementLink070]
  LockAngle = false
  _ConstraintType = 37
  _Parent = -> Constraints
FEATURE [App::FeaturePython] ElementLink069  label="_Element054"  # link proxy (typed FeaturePython)
  LinkTransform = true
  LinkedObject = -> _Element054
  _Parent = -> Constraint035
FEATURE [Part::FeaturePython] _Element054  # link proxy (typed FeaturePython)
  Detach = false
  LinkTransform = true
  LinkedObject = -> Link011 [Pad001.Face2]
  _Parent = -> Elements
FEATURE [App::FeaturePython] ElementLink070  label="_Element048"  # link proxy (typed FeaturePython)
  LinkTransform = true
  LinkedObject = -> _Element048
  _Parent = -> Constraint035
FEATURE [Part::FeaturePython] _Element055  # link proxy (typed FeaturePython)
  Detach = false
  LinkTransform = true
  LinkedObject = -> Link011 [Pad001.Face4]
  _Parent = -> Elements
FEATURE [Part::FeaturePython] _Element056  # link proxy (typed FeaturePython)
  Detach = false
  LinkTransform = true
  LinkedObject = -> Link009 [Pocket006.Face35]
  _Parent = -> Elements
FEATURE [App::FeaturePython] Constraint037  label="PlaneAlignment036"  # WARN: FeaturePython — macro-defined, semantics opaque (R4)
  Angle = 0
  AnglePitch = 0
  AngleRoll = 0
  Cascade = false
  Disabled = false
  Group = -> [ElementLink073,ElementLink074]
  LockAngle = false
  _ConstraintType = 37
  _Parent = -> Constraints
FEATURE [App::FeaturePython] ElementLink073  label="_Element057"  # link proxy (typed FeaturePython)
  LinkTransform = true
  LinkedObject = -> _Element057
  _Parent = -> Constraint037
FEATURE [Part::FeaturePython] _Element057  # link proxy (typed FeaturePython)
  Detach = false
  LinkTransform = true
  LinkedObject = -> Link010 [LinearPattern.Face4]
  _Parent = -> Elements
FEATURE [App::FeaturePython] ElementLink074  label="_Element058"  # link proxy (typed FeaturePython)
  LinkTransform = true
  LinkedObject = -> _Element058
  _Parent = -> Constraint037
FEATURE [Part::FeaturePython] _Element058  # link proxy (typed FeaturePython)
  Detach = false
  LinkTransform = true
  LinkedObject = -> Link011 [Pad001.Face5]
  _Parent = -> Elements
FEATURE [App::FeaturePython] Constraint038  label="PlaneAlignment037"  # WARN: FeaturePython — macro-defined, semantics opaque (R4)
  Angle = 0
  AnglePitch = 0
  AngleRoll = 0
  Cascade = false
  Disabled = false
  Group = -> [ElementLink075,ElementLink076]
  LockAngle = false
  _ConstraintType = 37
  _Parent = -> Constraints
FEATURE [App::FeaturePython] ElementLink075  label="_Element059"  # link proxy (typed FeaturePython)
  LinkTransform = true
  LinkedObject = -> _Element059
  _Parent = -> Constraint038
FEATURE [Part::FeaturePython] _Element059  # link proxy (typed FeaturePython)
  Detach = false
  LinkTransform = true
  LinkedObject = -> Link010 [LinearPattern.Face5]
  _Parent = -> Elements
FEATURE [App::FeaturePython] ElementLink076  label="_Element060"  # link proxy (typed FeaturePython)
  LinkTransform = true
  LinkedObject = -> _Element060
  _Parent = -> Constraint038
FEATURE [Part::FeaturePython] _Element060  # link proxy (typed FeaturePython)
  Detach = false
  LinkTransform = true
  LinkedObject = -> Link012 [Pocket003.Face11]
  _Parent = -> Elements
FEATURE [App::FeaturePython] Constraint039  label="PlaneAlignment038"  # WARN: FeaturePython — macro-defined, semantics opaque (R4)
  Angle = 0
  AnglePitch = 0
  AngleRoll = 0
  Cascade = false
  Disabled = false
  Group = -> [ElementLink077,ElementLink078]
  LockAngle = false
  _ConstraintType = 37
  _Parent = -> Constraints
FEATURE [App::FeaturePython] ElementLink077  label="_Element061"  # link proxy (typed FeaturePython)
  LinkTransform = true
  LinkedObject = -> _Element061
  _Parent = -> Constraint039
FEATURE [Part::FeaturePython] _Element061  # link proxy (typed FeaturePython)
  Detach = false
  LinkTransform = true
  LinkedObject = -> Link012 [Pocket003.Face10]
  _Parent = -> Elements
FEATURE [App::FeaturePython] ElementLink078  label="_Element050"  # link proxy (typed FeaturePython)
  LinkTransform = true
  LinkedObject = -> _Element050
  _Parent = -> Constraint039
FEATURE [App::FeaturePython] Constraint040  label="PlaneAlignment039"  # WARN: FeaturePython — macro-defined, semantics opaque (R4)
  Angle = 0
  AnglePitch = 0
  AngleRoll = 0
  Cascade = false
  Disabled = false
  Group = -> [ElementLink079,ElementLink080]
  LockAngle = false
  _ConstraintType = 37
  _Parent = -> Constraints
FEATURE [App::FeaturePython] ElementLink079  label="_Element052"  # link proxy (typed FeaturePython)
  LinkTransform = true
  LinkedObject = -> _Element052
  _Parent = -> Constraint040
FEATURE [App::FeaturePython] ElementLink080  label="_Element054"  # link proxy (typed FeaturePython)
  LinkTransform = true
  LinkedObject = -> _Element054
  _Parent = -> Constraint040
FEATURE [App::FeaturePython] Constraint041  label="PlaneAlignment040"  # WARN: FeaturePython — macro-defined, semantics opaque (R4)
  Angle = 0
  AnglePitch = 0
  AngleRoll = 0
  Cascade = false
  Disabled = false
  Group = -> [ElementLink081,ElementLink082]
  LockAngle = false
  _ConstraintType = 37
  _Parent = -> Constraints
FEATURE [App::FeaturePython] ElementLink081  label="_Element062"  # link proxy (typed FeaturePython)
  LinkTransform = true
  LinkedObject = -> _Element062
  _Parent = -> Constraint041
FEATURE [Part::FeaturePython] _Element062  # link proxy (typed FeaturePython)
  Detach = false
  LinkTransform = true
  LinkedObject = -> Link005 [Pocket005.Face30]
  _Parent = -> Elements
FEATURE [App::FeaturePython] ElementLink082  label="_Element026"  # link proxy (typed FeaturePython)
  LinkTransform = true
  LinkedObject = -> _Element026
  _Parent = -> Constraint041
FEATURE [App::FeaturePython] Constraint042  label="PlaneAlignment041"  # WARN: FeaturePython — macro-defined, semantics opaque (R4)
  Angle = 0
  AnglePitch = 0
  AngleRoll = 0
  Cascade = false
  Disabled = false
  Group = -> [ElementLink083,ElementLink084]
  LockAngle = false
  _ConstraintType = 37
  _Parent = -> Constraints
FEATURE [App::FeaturePython] ElementLink083  label="_Element055"  # link proxy (typed FeaturePython)
  LinkTransform = true
  LinkedObject = -> _Element055
  _Parent = -> Constraint042
FEATURE [App::FeaturePython] ElementLink084  label="_Element063"  # link proxy (typed FeaturePython)
  LinkTransform = true
  LinkedObject = -> _Element063
  _Parent = -> Constraint042
FEATURE [Part::FeaturePython] _Element063  # link proxy (typed FeaturePython)
  Detach = false
  LinkTransform = true
  LinkedObject = -> Link009 [Pocket005.Face31]
  _Parent = -> Elements
FEATURE [App::FeaturePython] Constraint043  label="PlaneAlignment042"  # WARN: FeaturePython — macro-defined, semantics opaque (R4)
  Angle = 0
  AnglePitch = 0
  AngleRoll = 0
  Cascade = false
  Disabled = false
  Group = -> [ElementLink085,ElementLink086]
  LockAngle = false
  _ConstraintType = 37
  _Parent = -> Constraints
FEATURE [App::FeaturePython] ElementLink085  label="_Element052"  # link proxy (typed FeaturePython)
  LinkTransform = true
  LinkedObject = -> _Element052
  _Parent = -> Constraint043
FEATURE [App::FeaturePython] ElementLink086  label="_Element054"  # link proxy (typed FeaturePython)
  LinkTransform = true
  LinkedObject = -> _Element054
  _Parent = -> Constraint043

RESOLVED EXTERNAL PARTS (link-assembly join: the EXTERNAL_REF files above that resolve inside this repo's crawl, each included once):
---- part parts/Base.FCStd = doc fcstd_425ba72cea9f ----
FCSTD DOCUMENT  (FreeCAD 0.21R33668 +26 (Git))
Label: Base
License: All rights reserved
LicenseURL: http://en.wikipedia.org/wiki/All_rights_reserved
objects: Sketcher::SketchObject×4, PartDesign::Pad×3, PartDesign::SubShapeBinder×2, PartDesign::Pocket×1, PartDesign::Body×1
note: 15 computed .brp shape members not serialized (recipe doc carries the construction recipe); baked Part::Feature solids carry a one-line shape summary decoded from their .brp
EXTERNAL_REF file=MG/mgn9c_13.FCStd obj=Body
EXTERNAL_REF file=MG/mgn9c_slide.FCStd obj=Body001
EXTERNAL_REF file=MG/Datasheet.FCStd obj=Spreadsheet

FEATURE [PartDesign::SubShapeBinder] Binder  label="Rail"
  BindCopyOnChange = 0
  BindMode = 0
  ClaimChildren = false
  Context = -> Body [Binder.]
  Fuse = false
  MakeFace = true
  OffsetFill = false
  OffsetIntersection = false
  OffsetJoinType = 0
  OffsetOpenResult = false
  PartialLoad = false
  Relative = true
  Support = -> [<external MG/mgn9c_13.FCStd>#Body[LinearPattern.]]
  _Version = 2
FEATURE [PartDesign::SubShapeBinder] Binder001  label="Slide"
  BindCopyOnChange = 0
  BindMode = 0
  ClaimChildren = false
  Context = -> Body [Binder001.]
  Fuse = false
  MakeFace = true
  OffsetFill = false
  OffsetIntersection = false
  OffsetJoinType = 0
  OffsetOpenResult = false
  PartialLoad = false
  Placement = pos=(12,-5.5,2) rot=(0,0,1;0rad)
  Relative = true
  Support = -> [<external MG/mgn9c_slide.FCStd>#Body001]
  _Version = 2
FEATURE [Sketcher::SketchObject] Sketch
  ExternalGeometry = -> [Binder]
  FullyConstrained = true
  MapMode = 5
  Support = -> [XY_Plane]
  expr: Constraints[22] = .Constraints.Strength
  expr: Constraints[30] = .Constraints.Strength
  sketch-geometry (13):
    g0: LineSegment StartX=0 StartY=9 StartZ=0 EndX=12.25 EndY=9 EndZ=0
    g1: LineSegment StartX=12.25 StartY=0 StartZ=0 EndX=0 EndY=0 EndZ=0
    g2: LineSegment StartX=0 StartY=0 StartZ=0 EndX=0 EndY=9 EndZ=0
    g3: LineSegment StartX=12.25 StartY=-3 StartZ=0 EndX=-3 EndY=-3 EndZ=0
    g4: LineSegment StartX=-3 StartY=-3 StartZ=0 EndX=-3 EndY=12 EndZ=0
    g5: LineSegment StartX=-3 StartY=12 StartZ=0 EndX=12.25 EndY=12 EndZ=0
    g6: LineSegment StartX=12.25 StartY=12 StartZ=0 EndX=12.25 EndY=-3 EndZ=0
    g7: LineSegment StartX=12.25 StartY=12 StartZ=0 EndX=12.25 EndY=9 EndZ=0
    g8: LineSegment StartX=12.25 StartY=-3 StartZ=0 EndX=12.25 EndY=0 EndZ=0
    g9: GeomPoint X=12.25 Y=4.5 Z=0
    g10: LineSegment StartX=0 StartY=4.5 StartZ=0 EndX=12.25 EndY=4.5 EndZ=0
    g11: GeomPoint X=9.25 Y=4.5 Z=0
    g12: LineSegment StartX=0 StartY=0 StartZ=0 EndX=12.25 EndY=0 EndZ=0
  constraints (34):
    c: Coincident(g1,g2)
    c: Coincident(g2,g0)
    c: Horizontal(g0)
    c: Horizontal(g1)
    c: Vertical(g2)
    c: Coincident(g0,g-3)
    c: PointOnObject(g1,g-4)
    c: Coincident(g3,g4)
    c: Coincident(g4,g5)
    c: Coincident(g5,g6)
    c: Coincident(g6,g3)
    c: Horizontal(g3)
    c: Horizontal(g5)
    c: Vertical(g4)
    c: Vertical(g6)
    c: PointOnObject(g0,g6)
    c: Coincident(g7,g5)
    c: Coincident(g7,g0)
    c: Coincident(g8,g3)
    c: Coincident(g8,g1)
    c: Vertical(g8)
    c: DistanceY(g8,g8) = 3  'Strength'
    c: DistanceX(g3,g1) = 3
    c: PointOnObject(g9,g6)
    c: PointOnObject(g10,g2)
    c: Coincident(g10,g9)
    c: PointOnObject(g-5,g10)
    c: Symmetric(g3,g5,g10)
    c: PointOnObject(g11,g-5)
    c: PointOnObject(g11,g10)
    c: DistanceX(g11,g9) = 3
    c: Coincident(g12,g2)
    c: Coincident(g12,g8)
    c: DistanceX(g0,g0) = 12.25  'RailOverlap'
FEATURE [PartDesign::Pad] Pad
  Direction = (0,0,1)
  Length = 6.5
  Length2 = 10
  Profile = -> Sketch
  ReferenceAxis = -> Sketch [N_Axis]
  Type = 0
  expr: Length = <<Datasheet>>#<<mgn9c>>.Dim_Hr
FEATURE [Sketcher::SketchObject] Sketch001
  ExternalGeometry = -> [Pad]
  FullyConstrained = true
  MapMode = 5
  Placement = pos=(-3,0,0) rot=(0.57735,-0.57735,-0.57735;2.0944rad)
  Support = -> [Pad]
  sketch-geometry (4):
    g0: LineSegment StartX=-12 StartY=0 StartZ=0 EndX=3 EndY=0 EndZ=0
    g1: LineSegment StartX=3 StartY=0 StartZ=0 EndX=3 EndY=-2 EndZ=0
    g2: LineSegment StartX=3 StartY=-2 StartZ=0 EndX=-12 EndY=-2 EndZ=0
    g3: LineSegment StartX=-12 StartY=-2 StartZ=0 EndX=-12 EndY=0 EndZ=0
  constraints (10):
    c: Coincident(g0,g1)
    c: Coincident(g1,g2)
    c: Coincident(g2,g3)
    c: Coincident(g3,g0)
    c: Horizontal(g2)
    c: Vertical(g1)
    c: Vertical(g3)
    c: Coincident(g0,g-4)
    c: Coincident(g0,g-4)
    c: DistanceY(g1,g1) = 2  'PCB_Thickness'
FEATURE [PartDesign::Pad] Pad001
  BaseFeature = -> Pad
  Direction = (-1,0,0)
  Length = 3
  Length2 = 10
  Profile = -> Sketch001
  ReferenceAxis = -> Sketch001 [N_Axis]
  Reversed = true
  Type = 0
  expr: Length = <<Sketch>>.Constraints.Strength
FEATURE [Sketcher::SketchObject] Sketch002
  ExternalGeometry = -> [Pad001,Binder]
  FullyConstrained = true
  MapMode = 5
  Placement = pos=(0,0,-2) rot=(1,0,0;3.14159rad)
  Support = -> [Pad001]
  sketch-geometry (5):
    g0: LineSegment StartX=-3 StartY=-12 StartZ=0 EndX=12.25 EndY=-12 EndZ=0
    g1: LineSegment StartX=12.25 StartY=-12 StartZ=0 EndX=12.25 EndY=3 EndZ=0
    g2: LineSegment StartX=12.25 StartY=3 StartZ=0 EndX=-3 EndY=3 EndZ=0
    g3: LineSegment StartX=-3 StartY=3 StartZ=0 EndX=-3 EndY=-12 EndZ=0
    g4: Circle CenterX=7.5 CenterY=-4.5 CenterZ=0 NormalX=0 NormalY=0 NormalZ=1 AngleXU=0 Radius=1.75
  constraints (12):
    c: Coincident(g0,g1)
    c: Coincident(g1,g2)
    c: Coincident(g2,g3)
    c: Coincident(g3,g0)
    c: Horizontal(g0)
    c: Horizontal(g2)
    c: Vertical(g1)
    c: Vertical(g3)
    c: Coincident(g0,g-5)
    c: Coincident(g1,g-4)
    c: Coincident(g4,g-7)
    c: PointOnObject(g-6,g4)
FEATURE [PartDesign::Pad] Pad002
  BaseFeature = -> Pad001
  Direction = (0,0,-1)
  Length = 6
  Length2 = 10
  Profile = -> Sketch002
  ReferenceAxis = -> Sketch002 [N_Axis]
  Type = 0
  expr: Length = 6
FEATURE [Sketcher::SketchObject] Sketch003
  ExternalGeometry = -> [Pad002]
  FullyConstrained = true
  MapMode = 5
  Placement = pos=(0,0,-8) rot=(1,0,0;3.14159rad)
  Support = -> [Pad002]
  expr: Constraints[1] = <<Datasheet>>#<<mgn9c>>.Dim_D
  sketch-geometry (1):
    g0: Circle CenterX=7.5 CenterY=-4.5 CenterZ=0 NormalX=0 NormalY=0 NormalZ=1 AngleXU=0 Radius=3
  constraints (2):
    c: Coincident(g0,g-3)
    c: Diameter(g0) = 6
FEATURE [PartDesign::Pocket] Pocket
  BaseFeature = -> Pad002
  Direction = (0,0,1)
  Length = 5
  Length2 = 5
  Profile = -> Sketch003
  ReferenceAxis = -> Sketch003 [N_Axis]
  Type = 0
FEATURE [PartDesign::Body] Body  label="Base_PCB"
  Group = -> [Sketch,Binder001,Binder,Pad,Sketch001,Pad001,Sketch002,Pad002,Sketch003,Pocket]
  Origin = -> Origin
  Tip = -> Pocket
---- part parts/Joystick_Holder.FCStd = doc fcstd_c2c9535a4b80 ----
FCSTD DOCUMENT  (FreeCAD 0.21R33668 +26 (Git))
Label: Joystick_Holder
License: All rights reserved
LicenseURL: http://en.wikipedia.org/wiki/All_rights_reserved
objects: Sketcher::SketchObject×6, PartDesign::Pad×4, PartDesign::SubShapeBinder×2, PartDesign::Pocket×2, PartDesign::Body×1
note: 21 computed .brp shape members not serialized (recipe doc carries the construction recipe); baked Part::Feature solids carry a one-line shape summary decoded from their .brp
EXTERNAL_REF file=MG/mgn9c_slide.FCStd obj=Body001
EXTERNAL_REF file=R202.FCStd obj=Revolution
EXTERNAL_REF file=MG/Datasheet.FCStd obj=Spreadsheet
EXTERNAL_REF file=NormalConnectorMagnet.FCStd obj=Sketch002
EXTERNAL_REF file=NormalConnectorMagnet.FCStd obj=Pad002
EXTERNAL_REF file=NormalConnectorMagnet.FCStd obj=Sketch003

FEATURE [PartDesign::SubShapeBinder] Binder  label="Slide"
  BindCopyOnChange = 0
  BindMode = 0
  ClaimChildren = false
  Context = -> Body [Binder.]
  Fuse = false
  MakeFace = true
  OffsetFill = false
  OffsetIntersection = false
  OffsetJoinType = 0
  OffsetOpenResult = false
  PartialLoad = false
  Placement = pos=(0,0,0) rot=(0,0,1;1.5708rad)
  Relative = true
  Support = -> [<external MG/mgn9c_slide.FCStd>#Body001]
  _Version = 2
FEATURE [PartDesign::SubShapeBinder] Binder001  label="Joystick"
  BindCopyOnChange = 0
  BindMode = 0
  ClaimChildren = false
  Context = -> Body [Binder001.]
  Fuse = false
  MakeFace = true
  OffsetFill = false
  OffsetIntersection = false
  OffsetJoinType = 0
  OffsetOpenResult = false
  PartialLoad = false
  Placement = pos=(-16.5,16.5,-29.5) rot=(0,0,-1;1.5708rad)
  Relative = true
  Support = -> [<external R202.FCStd>#Revolution]
  _Version = 2
FEATURE [Sketcher::SketchObject] Sketch
  ExternalGeometry = -> [Binder001]
  FullyConstrained = true
  MapMode = 5
  Placement = pos=(-16.5,16.5,0) rot=(0,0,-1;1.5708rad)
  Support = -> [Binder001]
  sketch-geometry (17):
    g0: LineSegment StartX=-20.2 StartY=25.2 StartZ=0 EndX=20.2 EndY=25.2 EndZ=0
    g1: LineSegment StartX=20.2 StartY=25.2 StartZ=0 EndX=20.2 EndY=20.2 EndZ=0
    g2: LineSegment StartX=20.2 StartY=20.2 StartZ=0 EndX=-20.2 EndY=20.2 EndZ=0
    g3: LineSegment StartX=-20.2 StartY=20.2 StartZ=0 EndX=-20.2 EndY=25.2 EndZ=0
    g4: LineSegment StartX=-20.2 StartY=20.2 StartZ=0 EndX=-20.2 EndY=-16.25 EndZ=0
    g5: LineSegment StartX=-12.3 StartY=-16.25 StartZ=0 EndX=-12.3 EndY=-12.4483 EndZ=0
    g6: ArcOfCircle CenterX=-16.25 CenterY=-16.25 CenterZ=0 NormalX=0 NormalY=0 NormalZ=1 AngleXU=0 Radius=3.95 StartAngle=3.14159 EndAngle=6.28319
    g7: ArcOfCircle CenterX=0 CenterY=-1.78e-14 CenterZ=0 NormalX=0 NormalY=0 NormalZ=1 AngleXU=0 Radius=17.5 StartAngle=5.4918 EndAngle=10.2162
    g8: LineSegment StartX=12.3 StartY=-12.4483 StartZ=0 EndX=12.3 EndY=-16.25 EndZ=0
    g9: ArcOfCircle CenterX=16.25 CenterY=-16.25 CenterZ=0 NormalX=0 NormalY=0 NormalZ=1 AngleXU=0 Radius=3.95 StartAngle=3.14159 EndAngle=6.28319
    g10: LineSegment StartX=20.2 StartY=20.2 StartZ=0 EndX=20.2 EndY=-16.25 EndZ=0
    g11: Circle CenterX=-16.25 CenterY=16.25 CenterZ=0 NormalX=0 NormalY=0 NormalZ=1 AngleXU=0 Radius=1
    g12: Circle CenterX=16.25 CenterY=16.25 CenterZ=0 NormalX=0 NormalY=0 NormalZ=1 AngleXU=0 Radius=1
    g13: Circle CenterX=16.25 CenterY=-16.25 CenterZ=0 NormalX=0 NormalY=0 NormalZ=1 AngleXU=0 Radius=1
    g14: Circle CenterX=-16.25 CenterY=-16.25 CenterZ=0 NormalX=0 NormalY=0 NormalZ=1 AngleXU=0 Radius=1
    g15: GeomPoint X=-16.25 Y=-17.25 Z=0
    g16: GeomPoint X=16.25 Y=-15.25 Z=0
  constraints (39):
    c: Coincident(g0,g1)
    c: Coincident(g1,g2)
    c: Coincident(g2,g3)
    c: Coincident(g3,g0)
    c: Horizontal(g0)
    c: Vertical(g1)
    c: Vertical(g3)
    c: Coincident(g1,g-8)
    c: Coincident(g2,g-8)
    c: DistanceY(g3,g3) = 5  'Strength'
    c: Coincident(g4,g3)
    c: Vertical(g4)
    c: PointOnObject(g5,g-9)
    c: Vertical(g5)
    c: Coincident(g6,g-5)
    c: Coincident(g6,g4)
    c: Horizontal(g4,g6)
    c: Tangent(g6,g5) = -1.5708
    c: Coincident(g7,g-9)
    c: Coincident(g7,g5)
    c: Coincident(g8,g7)
    c: Coincident(g9,g-6)
    c: Tangent(g9,g-7) = 1.5708
    c: Tangent(g9,g8) = -1.5708
    c: Horizontal(g8,g9)
    c: Coincident(g10,g1)
    c: Coincident(g10,g9)
    c: Coincident(g11,g-4)
    c: Tangent(g11,g-4)
    c: Coincident(g12,g-3)
    c: Tangent(g12,g-3)
    c: Coincident(g13,g9)
    c: Coincident(g14,g6)
    c: PointOnObject(g15,g-5)
    c: PointOnObject(g15,g14)
    c: PointOnObject(g16,g-6)
    c: PointOnObject(g16,g13)
    c: Vertical(g15,g6)
    c: Vertical(g16,g9)
FEATURE [PartDesign::Pad] Pad
  Direction = (0,0,1)
  Length = 3
  Length2 = 10
  Placement = pos=(-16.5,16.5,-29.5) rot=(0,0,-1;1.5708rad)
  Profile = -> Sketch
  ReferenceAxis = -> Sketch [N_Axis]
  Type = 0
FEATURE [Sketcher::SketchObject] Sketch001
  ExternalGeometry = -> [Pad]
  FullyConstrained = true
  MapMode = 5
  Placement = pos=(8.7,16.5,-29.5) rot=(0.57735,0.57735,0.57735;2.0944rad)
  Support = -> [Pad]
  expr: .Constraints.Rad = 3
  expr: Constraints[25] = .Constraints.Rad
  expr: Constraints[26] = .Constraints.Rad
  expr: Constraints[27] = .Constraints.Rad
  expr: Constraints[30] = <<Datasheet>>#<<mgn9c>>.Dim_C
  expr: Constraints[31] = <<Datasheet>>#<<mgn9c>>.Dim_B
  expr: Constraints[8] = <<Datasheet>>#<<mgn9c>>.Dim_L1
  expr: Constraints[9] = <<Datasheet>>#<<mgn9c>>.Dim_W
  sketch-geometry (14):
    g0: LineSegment StartX=-9.45 StartY=9.5 StartZ=0 EndX=9.45 EndY=9.5 EndZ=0
    g1: LineSegment StartX=9.45 StartY=9.5 StartZ=0 EndX=9.45 EndY=29.5 EndZ=0
    g2: LineSegment StartX=9.45 StartY=29.5 StartZ=0 EndX=-9.45 EndY=29.5 EndZ=0
    g3: LineSegment StartX=-9.45 StartY=29.5 StartZ=0 EndX=-9.45 EndY=9.5 EndZ=0
    g4: GeomPoint X=1.9e-15 Y=29.5 Z=0
    g5: Circle CenterX=-5 CenterY=27 CenterZ=0 NormalX=0 NormalY=0 NormalZ=1 AngleXU=0 Radius=1.5
    g6: Circle CenterX=5 CenterY=27 CenterZ=0 NormalX=0 NormalY=0 NormalZ=1 AngleXU=0 Radius=1.5
    g7: Circle CenterX=-5 CenterY=12 CenterZ=0 NormalX=0 NormalY=0 NormalZ=1 AngleXU=0 Radius=1.5
    g8: Circle CenterX=5 CenterY=12 CenterZ=0 NormalX=0 NormalY=0 NormalZ=1 AngleXU=0 Radius=1.5
    g9: LineSegment StartX=-5 StartY=12 StartZ=0 EndX=5 EndY=12 EndZ=0
    g10: LineSegment StartX=5 StartY=12 StartZ=0 EndX=5 EndY=27 EndZ=0
    g11: LineSegment StartX=5 StartY=27 StartZ=0 EndX=-5 EndY=27 EndZ=0
    g12: LineSegment StartX=-5 StartY=27 StartZ=0 EndX=-5 EndY=12 EndZ=0
    g13: GeomPoint X=1.8e-15 Y=19.5 Z=0
  constraints (32):
    c: Coincident(g0,g1)
    c: Coincident(g1,g2)
    c: Coincident(g2,g3)
    c: Coincident(g3,g0)
    c: Horizontal(g0)
    c: Horizontal(g2)
    c: Vertical(g1)
    c: Vertical(g3)
    c: DistanceX(g2,g2) = 18.9
    c: DistanceY(g1,g1) = 20
    c: Symmetric(g-3,g-4,g4)
    c: Symmetric(g2,g1,g4)
    c: Coincident(g9,g10)
    c: Coincident(g10,g11)
    c: Coincident(g11,g12)
    c: Coincident(g12,g9)
    c: Horizontal(g9)
    c: Horizontal(g11)
    c: Vertical(g10)
    c: Vertical(g12)
    c: Coincident(g9,g7)
    c: Coincident(g10,g6)
    c: Coincident(g5,g11)
    c: Coincident(g8,g9)
    c: Diameter(g7) = 3  'Rad'
    c: Diameter(g8) = 3
    c: Diameter(g6) = 3
    c: Diameter(g5) = 3
    c: Symmetric(g1,g0,g13)
    c: Symmetric(g7,g6,g13)
    c: DistanceX(g11,g11) = 10
    c: DistanceY(g10,g10) = 15
FEATURE [PartDesign::Pad] Pad001
  BaseFeature = -> Pad
  Direction = (1,4e-16,0)
  Length = 5
  Length2 = 10
  Placement = pos=(-16.5,16.5,-29.5) rot=(0,0,-1;1.5708rad)
  Profile = -> Sketch001
  ReferenceAxis = -> Sketch001 [N_Axis]
  Reversed = true
  Type = 0
  expr: Length = <<Sketch>>.Constraints.Strength
FEATURE [Sketcher::SketchObject] Sketch002
  ExternalGeometry = -> [Pad001]
  FullyConstrained = true
  MapMode = 5
  Placement = pos=(3.7,16.5,-29.5) rot=(0.57735,-0.57735,-0.57735;2.0944rad)
  Support = -> [Pad001]
  sketch-geometry (4):
    g0: LineSegment StartX=-9.45 StartY=9.5 StartZ=0 EndX=-7.45 EndY=9.5 EndZ=0
    g1: LineSegment StartX=-7.45 StartY=9.5 StartZ=0 EndX=-7.45 EndY=7.5 EndZ=0
    g2: LineSegment StartX=-7.45 StartY=7.5 StartZ=0 EndX=-9.45 EndY=7.5 EndZ=0
    g3: LineSegment StartX=-9.45 StartY=7.5 StartZ=0 EndX=-9.45 EndY=9.5 EndZ=0
  constraints (11):
    c: Coincident(g0,g1)
    c: Coincident(g1,g2)
    c: Coincident(g2,g3)
    c: Coincident(g3,g0)
    c: Horizontal(g0)
    c: Horizontal(g2)
    c: Vertical(g1)
    c: Vertical(g3)
    c: DistanceX(g2,g2) = 2
    c: Coincident(g0,g-3)
    c: DistanceY(g1,g1) = 2
FEATURE [PartDesign::Pad] Pad002
  BaseFeature = -> Pad001
  Direction = (-1,-4e-16,0)
  Length = 13
  Length2 = 10
  Placement = pos=(-16.5,16.5,-29.5) rot=(0,0,-1;1.5708rad)
  Profile = -> Sketch002
  ReferenceAxis = -> Sketch002 [N_Axis]
  Reversed = true
  Type = 0
  expr: Length = <<Pad001>>.Length + <<Datasheet>>#<<mgn9c>>.Dim_H - <<Datasheet>>#<<mgn9c>>.Dim_H1
FEATURE [Sketcher::SketchObject] Sketch003
  ExternalGeometry = -> [Pad002]
  FullyConstrained = true
  MapMode = 5
  Placement = pos=(16.7,16.5,-29.5) rot=(0.57735,0.57735,0.57735;2.0944rad)
  Support = -> [Pad002]
  expr: Constraints[17] = <<NormalConnectorMagnet>>#<<Sketch002>>.Constraints.SlideToMagnetCenter
  sketch-geometry (13):
    g0: LineSegment StartX=9.45 StartY=9.5 StartZ=0 EndX=4.45 EndY=9.5 EndZ=0
    g1: LineSegment StartX=4.45 StartY=9.5 StartZ=0 EndX=4.45 EndY=2.35 EndZ=0
    g2: LineSegment StartX=4.45 StartY=2.35 StartZ=0 EndX=9.45 EndY=2.35 EndZ=0
    g3: LineSegment StartX=9.45 StartY=2.35 StartZ=0 EndX=9.45 EndY=9.5 EndZ=0
    g4: Circle CenterX=6.95 CenterY=4.85 CenterZ=0 NormalX=0 NormalY=0 NormalZ=1 AngleXU=0 Radius=1.5
    g5: GeomPoint X=8.45 Y=4.85 Z=0
    g6: GeomPoint X=6.95 Y=3.35 Z=0
    g7: LineSegment StartX=6.95 StartY=3.35 StartZ=0 EndX=6.95 EndY=2.35 EndZ=0
    g8: LineSegment StartX=7.45 StartY=7.5 StartZ=0 EndX=4.45 EndY=6.35 EndZ=0
    g9: LineSegment StartX=4.45 StartY=6.35 StartZ=0 EndX=4.45 EndY=2.35 EndZ=0
    g10: GeomPoint X=6.95 Y=6.35 Z=0
    g11: LineSegment StartX=7.45 StartY=9.5 StartZ=0 EndX=9.45 EndY=9.5 EndZ=0
    g12: LineSegment StartX=7.45 StartY=7.5 StartZ=0 EndX=7.45 EndY=9.5 EndZ=0
  constraints (32):
    c: Coincident(g0,g1)
    c: Coincident(g1,g2)
    c: Coincident(g2,g3)
    c: Coincident(g3,g0)
    c: Horizontal(g0)
    c: Horizontal(g2)
    c: Vertical(g1)
    c: Vertical(g3)
    c: PointOnObject(g-3,g3)
    c: PointOnObject(g-4,g0)
    c: Diameter(g4) = 3
    c: PointOnObject(g5,g4)
    c: DistanceX(g5,g0) = 1
    c: PointOnObject(g6,g4)
    c: DistanceY(g2,g6) = 1
    c: Horizontal(g5,g4)
    c: Vertical(g4,g6)
    c: DistanceY(g4,g0) = 4.65
    c: Coincident(g7,g6)
    c: Vertical(g7)
    c: Symmetric(g1,g2,g7)
    c: Coincident(g8,g-4)
    c: PointOnObject(g8,g1)
    c: Coincident(g9,g8)
    c: Coincident(g9,g2)
    c: PointOnObject(g10,g4)
    c: Vertical(g10,g4)
    c: Horizontal(g8,g10)
    c: Coincident(g12,g11)
    c: Coincident(g11,g-4)
    c: Coincident(g0,g11)
    c: Coincident(g8,g12)
FEATURE [PartDesign::Pad] Pad003
  BaseFeature = -> Pad002
  Direction = (1,4e-16,0)
  Length = 2
  Length2 = 10
  Placement = pos=(-16.5,16.5,-29.5) rot=(0,0,-1;1.5708rad)
  Profile = -> Sketch003
  ReferenceAxis = -> Sketch003 [N_Axis]
  Reversed = true
  Type = 0
  expr: Length = <<NormalConnectorMagnet>>#<<Pad002>>.Length
FEATURE [Sketcher::SketchObject] Sketch004
  ExternalGeometry = -> [Pad003]
  FullyConstrained = true
  MapMode = 5
  Placement = pos=(14.7,16.5,-29.5) rot=(0.57735,-0.57735,-0.57735;2.0944rad)
  Support = -> [Pad003]
  expr: Constraints[1] = <<NormalConnectorMagnet>>#<<Sketch003>>.Constraints.MagnetDiameter
  sketch-geometry (1):
    g0: Circle CenterX=-6.95 CenterY=4.85 CenterZ=0 NormalX=0 NormalY=0 NormalZ=1 AngleXU=0 Radius=2
  constraints (2):
    c: Coincident(g0,g-3)
    c: Diameter(g0) = 4
FEATURE [PartDesign::Pocket] Pocket
  BaseFeature = -> Pad003
  Direction = (1,0,0)
  Length = 1
  Length2 = 5
  Placement = pos=(-16.5,16.5,-29.5) rot=(0,0,-1;1.5708rad)
  Profile = -> Sketch004
  ReferenceAxis = -> Sketch004 [N_Axis]
  Type = 0
FEATURE [Sketcher::SketchObject] Sketch005
  ExternalGeometry = -> [Pocket]
  FullyConstrained = true
  MapMode = 5
  Placement = pos=(3.7,16.5,-29.5) rot=(0.57735,-0.57735,-0.57735;2.0944rad)
  Support = -> [Pocket]
  expr: Constraints[1] = <<Datasheet>>#<<mgn9c>>.Dim_D
  expr: Constraints[5] = <<Datasheet>>#<<mgn9c>>.Dim_D
  expr: Constraints[6] = <<Datasheet>>#<<mgn9c>>.Dim_D
  expr: Constraints[7] = <<Datasheet>>#<<mgn9c>>.Dim_D
  sketch-geometry (14):
    g0: Circle CenterX=-5 CenterY=27 CenterZ=0 NormalX=0 NormalY=0 NormalZ=1 AngleXU=0 Radius=3
    g1: Circle CenterX=5 CenterY=27 CenterZ=0 NormalX=0 NormalY=0 NormalZ=1 AngleXU=0 Radius=3
    g2: Circle CenterX=5 CenterY=12 CenterZ=0 NormalX=0 NormalY=0 NormalZ=1 AngleXU=0 Radius=3
    g3: Circle CenterX=-5 CenterY=12 CenterZ=0 NormalX=0 NormalY=0 NormalZ=1 AngleXU=0 Radius=3
    g4: ArcOfCircle CenterX=-5 CenterY=12 CenterZ=0 NormalX=0 NormalY=0 NormalZ=1 AngleXU=0 Radius=3 StartAngle=2.26252e-07 EndAngle=3.14159
    g5: ArcOfCircle CenterX=5 CenterY=12 CenterZ=0 NormalX=0 NormalY=0 NormalZ=1 AngleXU=0 Radius=3 StartAngle=6.28318 EndAngle=9.42479
    g6: LineSegment StartX=2 StartY=9.5 StartZ=0 EndX=8 EndY=9.5 EndZ=0
    g7: LineSegment StartX=8 StartY=9.5 StartZ=0 EndX=8 EndY=12 EndZ=0
    g8: LineSegment StartX=8 StartY=12 StartZ=0 EndX=2 EndY=12 EndZ=0
    g9: LineSegment StartX=2 StartY=12 StartZ=0 EndX=2 EndY=9.5 EndZ=0
    g10: LineSegment StartX=-2 StartY=7.5 StartZ=0 EndX=-8 EndY=7.5 EndZ=0
    g11: LineSegment StartX=-8 StartY=7.5 StartZ=0 EndX=-8 EndY=12 EndZ=0
    g12: LineSegment StartX=-8 StartY=12 StartZ=0 EndX=-2 EndY=12 EndZ=0
    g13: LineSegment StartX=-2 StartY=12 StartZ=0 EndX=-2 EndY=7.5 EndZ=0
  constraints (36):
    c: Coincident(g0,g-3)
    c: Diameter(g0) = 6
    c: Coincident(g1,g-4)
    c: Coincident(g2,g-5)
    c: Coincident(g3,g-6)
    c: Diameter(g1) = 6
    c: Diameter(g2) = 6
    c: Diameter(g3) = 6
    c: Coincident(g4,g3)
    c: PointOnObject(g4,g3)
    c: Coincident(g5,g2)
    c: PointOnObject(g5,g2)
    c: Coincident(g6,g7)
    c: Coincident(g7,g8)
    c: Coincident(g8,g9)
    c: Coincident(g9,g6)
    c: Horizontal(g6)
    c: Horizontal(g8)
    c: Vertical(g7)
    c: Vertical(g9)
    c: Coincident(g7,g5)
    c: PointOnObject(g6,g-7)
    c: Coincident(g5,g8)
    c: Coincident(g10,g11)
    c: Coincident(g11,g12)
    c: Coincident(g12,g13)
    c: Coincident(g13,g10)
    c: Horizontal(g10)
    c: Horizontal(g12)
    c: Vertical(g11)
    c: Vertical(g13)
    c: Coincident(g11,g4)
    c: Coincident(g4,g12)
    c: Tangent(g13,g4)
    c: Tangent(g9,g5)
    c: PointOnObject(g-8,g10)
FEATURE [PartDesign::Pocket] Pocket001
  BaseFeature = -> Pocket
  Direction = (1,9e-16,0)
  Length = 3
  Length2 = 5
  Placement = pos=(-16.5,16.5,-29.5) rot=(0,0,-1;1.5708rad)
  Profile = -> Sketch005
  ReferenceAxis = -> Sketch005 [N_Axis]
  Type = 4
  expr: Length = <<Pad001>>.Length - 2 mm
FEATURE [PartDesign::Body] Body  label="JoystickHolder"
  Group = -> [Binder,Binder001,Sketch,Pad,Sketch001,Pad001,Sketch002,Pad002,Sketch003,Pad003,Sketch004,Pocket,Sketch005,Pocket001]
  Origin = -> Origin
  Placement = pos=(0,0,-4) rot=(0,0,1;0rad)
  Tip = -> Pocket001
---- part parts/MG/mgn9c_13.FCStd = doc fcstd_af4c73f2d28f ----
FCSTD DOCUMENT  (FreeCAD 0.21R33668 +26 (Git))
Label: mgn9c_13
License: All rights reserved
LicenseURL: http://en.wikipedia.org/wiki/All_rights_reserved
objects: Sketcher::SketchObject×2, App::Link×1, PartDesign::Pad×1, PartDesign::Pocket×1, PartDesign::LinearPattern×1, PartDesign::Body×1
note: 8 computed .brp shape members not serialized (recipe doc carries the construction recipe); baked Part::Feature solids carry a one-line shape summary decoded from their .brp
EXTERNAL_REF file=Datasheet.FCStd obj=Spreadsheet

FEATURE [App::Link] Link  label="mgn9c"
  LinkedObject = -> <external Datasheet.FCStd>#Spreadsheet
FEATURE [Sketcher::SketchObject] Sketch
  Base_Number_Holes = 13
  FullyConstrained = true
  MapMode = 5
  Support = -> [XY_Plane]
  expr: Constraints[10] = <<mgn9c>>.Dim_Wr
  sketch-geometry (4):
    g0: LineSegment StartX=0 StartY=0 StartZ=0 EndX=255 EndY=0 EndZ=0
    g1: LineSegment StartX=255 StartY=0 StartZ=0 EndX=255 EndY=9 EndZ=0
    g2: LineSegment StartX=255 StartY=9 StartZ=0 EndX=0 EndY=9 EndZ=0
    g3: LineSegment StartX=0 StartY=9 StartZ=0 EndX=0 EndY=0 EndZ=0
  constraints (11):
    c: Coincident(g0,g1)
    c: Coincident(g1,g2)
    c: Coincident(g2,g3)
    c: Coincident(g3,g0)
    c: Horizontal(g0)
    c: Horizontal(g2)
    c: Vertical(g1)
    c: Vertical(g3)
    c: Coincident(g0,g-1)
    c: DistanceX(g2,g2) = 255  'Rail_Length'
    c: DistanceY(g3,g3) = 9
FEATURE [PartDesign::Pad] Pad
  Direction = (0,0,1)
  Length = 6.5
  Length2 = 10
  Profile = -> Sketch
  ReferenceAxis = -> Sketch [N_Axis]
  Type = 0
  expr: Length = <<mgn9c>>.Dim_Hr
FEATURE [Sketcher::SketchObject] Sketch001
  FullyConstrained = true
  MapMode = 5
  Placement = pos=(0,0,6.5) rot=(0,0,1;0rad)
  Support = -> [Pad]
  expr: Constraints[0] = <<mgn9c>>.Dim_E
  expr: Constraints[1] = <<mgn9c>>.Dim_Wr / 2
  expr: Constraints[2] = <<mgn9c>>.Dim_d
  sketch-geometry (1):
    g0: Circle CenterX=7.5 CenterY=4.5 CenterZ=0 NormalX=0 NormalY=0 NormalZ=1 AngleXU=0 Radius=1.75
  constraints (3):
    c: DistanceX(g-1,g0) = 7.5
    c: DistanceY(g-1,g0) = 4.5
    c: Diameter(g0) = 3.5
FEATURE [PartDesign::Pocket] Pocket
  BaseFeature = -> Pad
  Direction = (0,0,-1)
  Length = 6.5
  Length2 = 5
  Profile = -> Sketch001
  ReferenceAxis = -> Sketch001 [N_Axis]
  Type = 0
  expr: Length = <<mgn9c>>.Dim_Hr
FEATURE [PartDesign::LinearPattern] LinearPattern
  BaseFeature = -> Pocket
  Direction = -> Sketch001 [H_Axis]
  Length = 240
  Occurrences = 13
  Originals = -> [Pocket]
  expr: Length = <<Sketch>>.Constraints.Rail_Length - <<mgn9c>>.Dim_E * 2
  expr: Occurrences = <<Sketch>>.Base_Number_Holes
FEATURE [PartDesign::Body] Body  label="Rail"
  Group = -> [Sketch,Pad,Sketch001,Pocket,LinearPattern]
  Origin = -> Origin
  Tip = -> LinearPattern
---- part parts/MG/mgn9c_slide.FCStd = doc fcstd_17b450fab925 ----
FCSTD DOCUMENT  (FreeCAD 0.21R33668 +26 (Git))
Label: mgn9c_slide
License: All rights reserved
LicenseURL: http://en.wikipedia.org/wiki/All_rights_reserved
objects: Sketcher::SketchObject×4, PartDesign::Pocket×3, App::Link×1, PartDesign::Pad×1, PartDesign::Body×1
note: 13 computed .brp shape members not serialized (recipe doc carries the construction recipe); baked Part::Feature solids carry a one-line shape summary decoded from their .brp
EXTERNAL_REF file=Datasheet.FCStd obj=Spreadsheet

FEATURE [App::Link] Link  label="mgn9c"
  LinkedObject = -> <external Datasheet.FCStd>#Spreadsheet
FEATURE [Sketcher::SketchObject] Sketch002
  FullyConstrained = true
  MapMode = 5
  Support = -> [XY_Plane001]
  expr: Constraints[10] = <<mgn9c>>.Dim_W
  expr: Constraints[9] = <<mgn9c>>.Dim_L
  sketch-geometry (4):
    g0: LineSegment StartX=0 StartY=0 StartZ=0 EndX=28.9 EndY=0 EndZ=0
    g1: LineSegment StartX=28.9 StartY=0 StartZ=0 EndX=28.9 EndY=20 EndZ=0
    g2: LineSegment StartX=28.9 StartY=20 StartZ=0 EndX=0 EndY=20 EndZ=0
    g3: LineSegment StartX=0 StartY=20 StartZ=0 EndX=0 EndY=0 EndZ=0
  constraints (11):
    c: Coincident(g0,g1)
    c: Coincident(g1,g2)
    c: Coincident(g2,g3)
    c: Coincident(g3,g0)
    c: Horizontal(g0)
    c: Horizontal(g2)
    c: Vertical(g1)
    c: Vertical(g3)
    c: Coincident(g0,g-1)
    c: DistanceX(g2,g2) = 28.9
    c: DistanceY(g1,g1) = 20
FEATURE [PartDesign::Pad] Pad001
  Direction = (0,0,1)
  Length = 8
  Length2 = 10
  Profile = -> Sketch002
  ReferenceAxis = -> Sketch002 [N_Axis]
  Type = 0
  expr: Length = <<mgn9c>>.Dim_H - <<mgn9c>>.Dim_H1
FEATURE [Sketcher::SketchObject] Sketch003
  ExternalGeometry = -> [Pad001]
  FullyConstrained = true
  MapMode = 5
  Placement = pos=(0,0,0) rot=(0.57735,-0.57735,-0.57735;2.0944rad)
  Support = -> [Pad001]
  expr: Constraints[10] = <<mgn9c>>.Dim_Hr - <<mgn9c>>.Dim_H1
  expr: Constraints[8] = <<mgn9c>>.Dim_N
  expr: Constraints[9] = <<mgn9c>>.Dim_N
  sketch-geometry (4):
    g0: LineSegment StartX=-14.5 StartY=0 StartZ=0 EndX=-5.5 EndY=0 EndZ=0
    g1: LineSegment StartX=-5.5 StartY=0 StartZ=0 EndX=-5.5 EndY=4.5 EndZ=0
    g2: LineSegment StartX=-5.5 StartY=4.5 StartZ=0 EndX=-14.5 EndY=4.5 EndZ=0
    g3: LineSegment StartX=-14.5 StartY=4.5 StartZ=0 EndX=-14.5 EndY=0 EndZ=0
  constraints (12):
    c: Coincident(g0,g1)
    c: Coincident(g1,g2)
    c: Coincident(g2,g3)
    c: Coincident(g3,g0)
    c: Horizontal(g0)
    c: Horizontal(g2)
    c: Vertical(g1)
    c: Vertical(g3)
    c: DistanceX(g-5,g0) = 5.5
    c: DistanceX(g0,g-6) = 5.5
    c: DistanceY(g1,g1) = 4.5
    c: PointOnObject(g0,g-5)
FEATURE [PartDesign::Pocket] Pocket001
  BaseFeature = -> Pad001
  Direction = (1,0,0)
  Length = 28.9
  Length2 = 5
  Profile = -> Sketch003
  ReferenceAxis = -> Sketch003 [N_Axis]
  Type = 0
  expr: Length = <<mgn9c>>.Dim_L
FEATURE [Sketcher::SketchObject] Sketch004
  ExternalGeometry = -> [Pocket001]
  FullyConstrained = true
  MapMode = 5
  Placement = pos=(0,0,8) rot=(0,0,1;0rad)
  Support = -> [Pocket001]
  expr: Constraints[17] = 3
  expr: Constraints[18] = 3
  expr: Constraints[19] = 3
  expr: Constraints[20] = 3
  expr: Constraints[8] = <<mgn9c>>.Dim_C
  expr: Constraints[9] = <<mgn9c>>.Dim_B
  sketch-geometry (9):
    g0: LineSegment StartX=9.45 StartY=17.5 StartZ=0 EndX=19.45 EndY=17.5 EndZ=0
    g1: LineSegment StartX=19.45 StartY=17.5 StartZ=0 EndX=19.45 EndY=2.5 EndZ=0
    g2: LineSegment StartX=19.45 StartY=2.5 StartZ=0 EndX=9.45 EndY=2.5 EndZ=0
    g3: LineSegment StartX=9.45 StartY=2.5 StartZ=0 EndX=9.45 EndY=17.5 EndZ=0
    g4: GeomPoint X=14.45 Y=10 Z=0
    g5: Circle CenterX=9.45 CenterY=17.5 CenterZ=0 NormalX=0 NormalY=0 NormalZ=1 AngleXU=0 Radius=1.5
    g6: Circle CenterX=19.45 CenterY=17.5 CenterZ=0 NormalX=0 NormalY=0 NormalZ=1 AngleXU=0 Radius=1.5
    g7: Circle CenterX=19.45 CenterY=2.5 CenterZ=0 NormalX=0 NormalY=0 NormalZ=1 AngleXU=0 Radius=1.5
    g8: Circle CenterX=9.45 CenterY=2.5 CenterZ=0 NormalX=0 NormalY=0 NormalZ=1 AngleXU=0 Radius=1.5
  constraints (21):
    c: Coincident(g0,g1)
    c: Coincident(g1,g2)
    c: Coincident(g2,g3)
    c: Coincident(g3,g0)
    c: Horizontal(g0)
    c: Horizontal(g2)
    c: Vertical(g1)
    c: Vertical(g3)
    c: DistanceX(g0,g0) = 10
    c: DistanceY(g1,g1) = 15
    c: DistanceY(g-4,g2) = 2.5
    c: Symmetric(g-3,g-4,g4)
    c: Symmetric(g1,g0,g4)
    c: Coincident(g5,g0)
    c: Coincident(g6,g0)
    c: Coincident(g7,g1)
    c: Coincident(g8,g2)
    c: Diameter(g8) = 3
    c: Diameter(g7) = 3
    c: Diameter(g6) = 3
    c: Diameter(g5) = 3
FEATURE [PartDesign::Pocket] Pocket002
  BaseFeature = -> Pocket001
  Direction = (0,0,-1)
  Length = 3
  Length2 = 5
  Profile = -> Sketch004
  ReferenceAxis = -> Sketch004 [N_Axis]
  Type = 0
FEATURE [Sketcher::SketchObject] Sketch005
  ExternalGeometry = -> [Pocket002]
  FullyConstrained = true
  MapMode = 5
  Placement = pos=(0,0,8) rot=(0,0,1;0rad)
  Support = -> [Pocket002]
  expr: Constraints[19] = <<mgn9c>>.Dim_L1
  sketch-geometry (9):
    g0: LineSegment StartX=0 StartY=20 StartZ=0 EndX=5 EndY=20 EndZ=0
    g1: LineSegment StartX=5 StartY=20 StartZ=0 EndX=5 EndY=0 EndZ=0
    g2: LineSegment StartX=5 StartY=0 StartZ=0 EndX=0 EndY=0 EndZ=0
    g3: LineSegment StartX=0 StartY=0 StartZ=0 EndX=0 EndY=20 EndZ=0
    g4: LineSegment StartX=28.9 StartY=0 StartZ=0 EndX=23.9 EndY=0 EndZ=0
    g5: LineSegment StartX=23.9 StartY=0 StartZ=0 EndX=23.9 EndY=20 EndZ=0
    g6: LineSegment StartX=23.9 StartY=20 StartZ=0 EndX=28.9 EndY=20 EndZ=0
    g7: LineSegment StartX=28.9 StartY=20 StartZ=0 EndX=28.9 EndY=0 EndZ=0
    g8: GeomPoint X=14.45 Y=0 Z=0
  constraints (22):
    c: Coincident(g0,g1)
    c: Coincident(g1,g2)
    c: Coincident(g2,g3)
    c: Coincident(g3,g0)
    c: Horizontal(g0)
    c: Horizontal(g2)
    c: Vertical(g1)
    c: Vertical(g3)
    c: Coincident(g0,g-3)
    c: PointOnObject(g1,g-1)
    c: Coincident(g4,g5)
    c: Coincident(g5,g6)
    c: Coincident(g6,g7)
    c: Coincident(g7,g4)
    c: Horizontal(g6)
    c: Vertical(g5)
    c: Vertical(g7)
    c: Symmetric(g2,g-4,g8)
    c: Symmetric(g4,g1,g8)
    c: DistanceX(g1,g4) = 18.9
    c: PointOnObject(g5,g-5)
    c: Coincident(g4,g-4)
FEATURE [PartDesign::Pocket] Pocket003
  BaseFeature = -> Pocket002
  Direction = (0,0,-1)
  Length = 0.1
  Length2 = 5
  Profile = -> Sketch005
  ReferenceAxis = -> Sketch005 [N_Axis]
  Type = 0
FEATURE [PartDesign::Body] Body001  label="Slide"
  Group = -> [Sketch002,Pad001,Sketch003,Pocket001,Sketch004,Pocket002,Sketch005,Pocket003]
  Origin = -> Origin001
  Tip = -> Pocket003
---- part parts/NormalConnector.FCStd = doc fcstd_c7b02f5a6e60 ----
FCSTD DOCUMENT  (FreeCAD 0.21R33668 +26 (Git))
Label: NormalConnector
License: All rights reserved
LicenseURL: http://en.wikipedia.org/wiki/All_rights_reserved
objects: Sketcher::SketchObject×7, PartDesign::Pocket×6, PartDesign::SubShapeBinder×4, PartDesign::Pad×1, PartDesign::Body×1
note: 26 computed .brp shape members not serialized (recipe doc carries the construction recipe); baked Part::Feature solids carry a one-line shape summary decoded from their .brp
EXTERNAL_REF file=MG/mgn9c_slide.FCStd obj=Body001
EXTERNAL_REF file=Base.FCStd obj=Sketch001
EXTERNAL_REF file=MG/Datasheet.FCStd obj=Spreadsheet
EXTERNAL_REF file=MG/mgn9c_13.FCStd obj=Body
EXTERNAL_REF file=OmniballConnector/OmniballConnector_7945.FCStd obj=Sketch002
EXTERNAL_REF file=OmniballConnector/OmniballConnector_7945.FCStd obj=Body

FEATURE [PartDesign::SubShapeBinder] Binder  label="Slide"
  BindCopyOnChange = 0
  BindMode = 0
  ClaimChildren = false
  Context = -> Body [Binder.]
  Fuse = false
  MakeFace = true
  OffsetFill = false
  OffsetIntersection = false
  OffsetJoinType = 0
  OffsetOpenResult = false
  PartialLoad = false
  Placement = pos=(-5,0,-2) rot=(0,0,1;0rad)
  Relative = true
  Support = -> [<external MG/mgn9c_slide.FCStd>#Body001]
  _Version = 2
FEATURE [PartDesign::SubShapeBinder] Binder001  label="Rail"
  BindCopyOnChange = 0
  BindMode = 0
  ClaimChildren = false
  Context = -> Body [Binder001.]
  Fuse = false
  MakeFace = true
  OffsetFill = false
  OffsetIntersection = false
  OffsetJoinType = 0
  OffsetOpenResult = false
  PartialLoad = false
  Placement = pos=(-5,5.5,-2) rot=(0,0,1;0rad)
  Relative = true
  Support = -> [<external MG/mgn9c_13.FCStd>#Body]
  _Version = 2
FEATURE [Sketcher::SketchObject] Sketch
  ExternalGeometry = -> [Binder,Binder001]
  FullyConstrained = true
  MapMode = 5
  Placement = pos=(0,0,0) rot=(0.57735,0.57735,0.57735;2.0944rad)
  Support = -> [YZ_Plane]
  expr: Constraints[108] = <<Datasheet>>#<<mgn9c>>.Dim_H1
  expr: Constraints[11] = 0.102 in
  expr: Constraints[20] = 0.118 in
  expr: Constraints[23] = 0.03 in
  expr: Constraints[24] = 0.236 in
  expr: Constraints[25] = 0.091 in
  expr: Constraints[27] = 0.266 in
  expr: Constraints[88] = <<Datasheet>>#<<mgn9c>>.Dim_E * 2 + <<Datasheet>>#<<mgn9c>>.Dim_P
  expr: Constraints[98] = 2 mm + <<Base>>#<<Sketch001>>.Constraints.PCB_Thickness
  sketch-geometry (44):
    g0: LineSegment StartX=2.9e-15 StartY=6 StartZ=0 EndX=2.9e-15 EndY=-4 EndZ=0
    g1: LineSegment StartX=14.5 StartY=-2 StartZ=0 EndX=-25.5 EndY=-2 EndZ=0
    g2: LineSegment StartX=-5.294 StartY=1.9944 StartZ=0 EndX=-2.7032 EndY=1.9944 EndZ=0
    g3: LineSegment StartX=-2.7032 StartY=1.9944 StartZ=0 EndX=-2.7032 EndY=-3.238 EndZ=0
    g4: LineSegment StartX=-2.7032 StartY=-3.238 StartZ=0 EndX=-5.294 EndY=-3.238 EndZ=0
    g5: LineSegment StartX=-5.294 StartY=-3.238 StartZ=0 EndX=-5.294 EndY=1.9944 EndZ=0
    g6: LineSegment StartX=-5.4972 StartY=2.7564 StartZ=0 EndX=-2.5 EndY=2.7564 EndZ=0
    g7: LineSegment StartX=-2.5 StartY=2.7564 StartZ=0 EndX=-2.5 EndY=1.9944 EndZ=0
    g8: LineSegment StartX=-2.5 StartY=1.9944 StartZ=0 EndX=-5.4972 EndY=1.9944 EndZ=0
    g9: LineSegment StartX=-5.4972 StartY=1.9944 StartZ=0 EndX=-5.4972 EndY=2.7564 EndZ=0
    g10: GeomPoint X=-3.9986 Y=1.9944 Z=0
    g11: Circle CenterX=-3.9986 CenterY=-2.8443 CenterZ=0 NormalX=0 NormalY=0 NormalZ=1 AngleXU=0 Radius=1.1557
    g12: GeomPoint X=-3.9986 Y=-4 Z=0
    g13: LineSegment StartX=-10.2912 StartY=1.9944 StartZ=0 EndX=-7.7004 EndY=1.9944 EndZ=0
    g14: LineSegment StartX=-7.7004 StartY=1.9944 StartZ=0 EndX=-7.7004 EndY=-3.238 EndZ=0
    g15: LineSegment StartX=-7.7004 StartY=-3.238 StartZ=0 EndX=-10.2912 EndY=-3.238 EndZ=0
    g16: LineSegment StartX=-10.2912 StartY=-3.238 StartZ=0 EndX=-10.2912 EndY=1.9944 EndZ=0
    g17: LineSegment StartX=-10.4944 StartY=2.7564 StartZ=0 EndX=-7.4972 EndY=2.7564 EndZ=0
    g18: LineSegment StartX=-7.4972 StartY=2.7564 StartZ=0 EndX=-7.4972 EndY=1.9944 EndZ=0
    g19: LineSegment StartX=-7.4972 StartY=1.9944 StartZ=0 EndX=-10.4944 EndY=1.9944 EndZ=0
    g20: LineSegment StartX=-10.4944 StartY=1.9944 StartZ=0 EndX=-10.4944 EndY=2.7564 EndZ=0
    g21: GeomPoint X=-8.9958 Y=1.9944 Z=0
    g22: Circle CenterX=-8.9958 CenterY=-2.8443 CenterZ=0 NormalX=0 NormalY=0 NormalZ=1 AngleXU=0 Radius=1.1557
    g23: GeomPoint X=-8.9958 Y=-4 Z=0
    g24: LineSegment StartX=-2.5 StartY=2.7564 StartZ=0 EndX=-2.5 EndY=1.9944 EndZ=0
    g25: LineSegment StartX=-2.5 StartY=1.9944 StartZ=0 EndX=-5.4972 EndY=1.9944 EndZ=0
    g26: LineSegment StartX=-5.4972 StartY=1.9944 StartZ=0 EndX=-5.4972 EndY=2.3754 EndZ=0
    g27: LineSegment StartX=-5.4972 StartY=2.3754 StartZ=0 EndX=-7.4972 EndY=2.3754 EndZ=0
    g28: LineSegment StartX=-7.4972 StartY=2.3754 StartZ=0 EndX=-7.4972 EndY=1.9944 EndZ=0
    g29: LineSegment StartX=-7.4972 StartY=1.9944 StartZ=0 EndX=-10.4944 EndY=1.9944 EndZ=0
    g30: LineSegment StartX=-10.4944 StartY=1.9944 StartZ=0 EndX=-10.4944 EndY=2.7564 EndZ=0
    g31: LineSegment StartX=-10.4944 StartY=2.7564 StartZ=0 EndX=-12.4944 EndY=2.7564 EndZ=0
    g32: LineSegment StartX=-12.4944 StartY=2.7564 StartZ=0 EndX=-12.4944 EndY=-4 EndZ=0
    g33: LineSegment StartX=-2.5 StartY=2.7564 StartZ=0 EndX=-2 EndY=2.7564 EndZ=0
    g34: LineSegment StartX=-2 StartY=2.7564 StartZ=0 EndX=-2 EndY=11 EndZ=0
    g35: LineSegment StartX=2.9e-15 StartY=-4 StartZ=0 EndX=-12.4944 EndY=-4 EndZ=0
    g36: LineSegment StartX=-2 StartY=11 StartZ=0 EndX=10 EndY=11 EndZ=0
    g37: LineSegment StartX=24 StartY=6 StartZ=0 EndX=24 EndY=41 EndZ=0
    g38: LineSegment StartX=24 StartY=41 StartZ=0 EndX=20 EndY=41 EndZ=0
    g39: LineSegment StartX=20 StartY=41 StartZ=0 EndX=10 EndY=11 EndZ=0
    g40: LineSegment StartX=2.9e-15 StartY=6 StartZ=0 EndX=24 EndY=6 EndZ=0
    g41: LineSegment StartX=-12.4944 StartY=2.7564 StartZ=0 EndX=-12.4944 EndY=-3.238 EndZ=0
    g42: LineSegment StartX=-12.4944 StartY=-3.238 StartZ=0 EndX=3.6e-15 EndY=-3.238 EndZ=0
    g43: LineSegment StartX=3.6e-15 StartY=-3.238 StartZ=0 EndX=2.9e-15 EndY=6 EndZ=0
  constraints (118):
    c: Coincident(g1,g-7)
    c: Horizontal(g1)
    c: DistanceX(g1,g1) = 40
    c: Coincident(g2,g3)
    c: Coincident(g3,g4)
    c: Coincident(g4,g5)
    c: Coincident(g5,g2)
    c: Horizontal(g2)
    c: Horizontal(g4)
    c: Vertical(g3)
    c: Vertical(g5)
    c: DistanceX(g2,g2) = 2.5908
    c: Coincident(g6,g7)
    c: Coincident(g7,g8)
    c: Coincident(g8,g9)
    c: Coincident(g9,g6)
    c: Horizontal(g6)
    c: Horizontal(g8)
    c: Vertical(g7)
    c: Vertical(g9)
    c: DistanceX(g6,g6) = 2.9972
    c: Symmetric(g8,g7,g10)
    c: Symmetric(g2,g2,g10)
    c: DistanceY(g7,g7) = 0.762
    c: DistanceY(g3,g6) = 5.9944
    c: Diameter(g11) = 2.3114
    c: DistanceX(g10,g12) = 0
    c: DistanceY(g12,g6) = 6.7564
    c: DistanceX(g11,g12) = 0
    c: Coincident(g13,g14)
    c: Coincident(g14,g15)
    c: Coincident(g15,g16)
    c: Coincident(g16,g13)
    c: Horizontal(g13)
    c: Horizontal(g15)
    c: Vertical(g14)
    c: Vertical(g16)
    c: Equal(g2,g13) = 2.5908
    c: Coincident(g17,g18)
    c: Coincident(g18,g19)
    c: Coincident(g19,g20)
    c: Coincident(g20,g17)
    c: Horizontal(g17)
    c: Horizontal(g19)
    c: Vertical(g18)
    c: Vertical(g20)
    c: Equal(g6,g17) = 2.9972
    c: Symmetric(g19,g18,g21)
    c: Symmetric(g13,g13,g21)
    c: Equal(g7,g18) = 0.762
    c: DistanceY(g14,g17) = 5.9944
    c: Equal(g11,g22) = 2.3114
    c: DistanceX(g21,g23) = 0
    c: DistanceY(g23,g17) = 6.7564
    c: DistanceX(g22,g23) = 0
    c: Coincident(g24,g6)
    c: Coincident(g24,g7)
    c: Coincident(g25,g24)
    c: Coincident(g25,g8)
    c: Coincident(g26,g25)
    c: Coincident(g27,g26)
    c: PointOnObject(g27,g18)
    c: Coincident(g28,g27)
    c: Coincident(g28,g18)
    c: Coincident(g29,g28)
    c: Coincident(g29,g19)
    c: Horizontal(g27)
    c: Symmetric(g6,g25,g26)
    c: Coincident(g30,g29)
    c: Coincident(g30,g17)
    c: Coincident(g31,g17)
    c: Horizontal(g31)
    c: DistanceX(g31,g31) = 2
    c: Coincident(g32,g31)
    c: Vertical(g32)
    c: DistanceX(g27,g27) = 2
    c: Coincident(g33,g24)
    c: DistanceX(g33,g33) = 0.5
    c: Horizontal(g33)
    c: Coincident(g34,g33)
    c: Vertical(g34)
    c: DistanceX(g33,g-5) = 2
    c: Coincident(g35,g32)
    c: Horizontal(g35)
    c: DistanceY(g0,g34) = 5
    c: Coincident(g36,g34)
    c: Horizontal(g36)
    c: Vertical(g37)
    c: DistanceY(g37,g37) = 35
    c: Coincident(g38,g37)
    c: Horizontal(g38)
    c: Coincident(g39,g38)
    c: Coincident(g36,g39)
    c: DistanceX(g36,g36) = 12
    c: Coincident(g40,g37)
    c: Horizontal(g40)
    c: Coincident(g0,g40)
    c: Coincident(g0,g-4)
    c: DistanceX(g-4,g37) = 4
    c: DistanceX(g35,g35) = 12.4944  'PCB_Edge_Distance_From_Slide_Side'
    c: DistanceX(g12,g0) = 3.9986  'Connector_Close_Distance'
    c: DistanceX(g23,g0) = 8.9958  'Connector_Far_Distance'
    c: PointOnObject(g38,g-6)
    c: Coincident(g0,g35)
    c: Vertical(g0)
    c: PointOnObject(g12,g35)
    c: PointOnObject(g12,g11)
    c: PointOnObject(g23,g35)
    c: DistanceY(g0,g-5) = 2
    c: PointOnObject(g23,g22)
    c: Coincident(g41,g31)
    c: Coincident(g42,g41)
    c: PointOnObject(g42,g0)
    c: Horizontal(g42)
    c: Coincident(g43,g42)
    c: Coincident(g43,g40)
    c: PointOnObject(g3,g42)
    c: PointOnObject(g41,g32)
FEATURE [PartDesign::Pad] Pad
  Direction = (1,-2e-16,3e-16)
  Length = 18.9
  Length2 = 10
  Placement = pos=(0,0,0) rot=(0.57735,0.57735,0.57735;2.0944rad)
  Profile = -> Sketch
  ReferenceAxis = -> Sketch [N_Axis]
  Type = 0
  expr: Length = <<Datasheet>>#<<mgn9c>>.Dim_L1
FEATURE [Sketcher::SketchObject] Sketch001
  ExternalGeometry = -> [Pad]
  FullyConstrained = true
  MapMode = 5
  Placement = pos=(-9e-16,-2,4e-16) rot=(-0.57735,-0.57735,0.57735;4.18879rad)
  Support = -> [Pad]
  expr: Constraints[10] = <<Datasheet>>#<<mgn9c>>.Dim_Wr + 2 mm
  sketch-geometry (4):
    g0: LineSegment StartX=-41 StartY=18.9 StartZ=0 EndX=-11 EndY=18.9 EndZ=0
    g1: LineSegment StartX=-11 StartY=18.9 StartZ=0 EndX=-11 EndY=11 EndZ=0
    g2: LineSegment StartX=-11 StartY=11 StartZ=0 EndX=-41 EndY=11 EndZ=0
    g3: LineSegment StartX=-41 StartY=11 StartZ=0 EndX=-41 EndY=18.9 EndZ=0
  constraints (11):
    c: Coincident(g0,g1)
    c: Coincident(g1,g2)
    c: Coincident(g2,g3)
    c: Coincident(g3,g0)
    c: Horizontal(g0)
    c: Horizontal(g2)
    c: Vertical(g1)
    c: Vertical(g3)
    c: Coincident(g0,g-4)
    c: PointOnObject(g1,g-3)
    c: DistanceY(g-3,g1) = 11
FEATURE [PartDesign::Pocket] Pocket
  BaseFeature = -> Pad
  Direction = (4e-16,1,-2e-16)
  Length = 5
  Length2 = 5
  Placement = pos=(0,0,0) rot=(0.57735,0.57735,0.57735;2.0944rad)
  Profile = -> Sketch001
  ReferenceAxis = -> Sketch001 [N_Axis]
  Type = 1
FEATURE [Sketcher::SketchObject] Sketch002
  ExternalGeometry = -> [Pocket]
  FullyConstrained = true
  MapMode = 5
  Placement = pos=(-1.15e-14,1.8e-14,41) rot=(0,0,-1;1.5708rad)
  Support = -> [Pocket]
  expr: Constraints[5] = <<Datasheet>>#<<mgn9c>>.Dim_H1 / 2 + <<Base>>#<<Sketch001>>.Constraints.PCB_Thickness
  expr: Constraints[7] = <<Datasheet>>#<<mgn9c>>.Dim_Wr
  sketch-geometry (9):
    g0: LineSegment StartX=-21 StartY=10 StartZ=0 EndX=-21 EndY=1 EndZ=0
    g1: LineSegment StartX=-21 StartY=1 StartZ=0 EndX=-24 EndY=1 EndZ=0
    g2: LineSegment StartX=-24 StartY=1 StartZ=0 EndX=-24 EndY=10 EndZ=0
    g3: GeomPoint X=-24 Y=5.5 Z=0
    g4: LineSegment StartX=-21 StartY=10 StartZ=0 EndX=-24 EndY=10 EndZ=0
    g5: LineSegment StartX=-24 StartY=1 StartZ=0 EndX=-21 EndY=1 EndZ=0
    g6: LineSegment StartX=-21 StartY=1 StartZ=0 EndX=-21 EndY=0 EndZ=0
    g7: LineSegment StartX=-21 StartY=0 StartZ=0 EndX=-24 EndY=0 EndZ=0
    g8: LineSegment StartX=-24 StartY=0 StartZ=0 EndX=-24 EndY=1 EndZ=0
  constraints (22):
    c: Coincident(g0,g1)
    c: Coincident(g1,g2)
    c: Horizontal(g1)
    c: Vertical(g0)
    c: Vertical(g2)
    c: DistanceX(g1,g1) = 3
    c: Symmetric(g2,g1,g3)
    c: DistanceY(g0,g0) = 9
    c: Horizontal(g4)
    c: Coincident(g5,g6)
    c: Coincident(g6,g7)
    c: Coincident(g7,g8)
    c: Coincident(g8,g5)
    c: Horizontal(g7)
    c: Vertical(g6)
    c: Vertical(g8)
    c: Coincident(g5,g1)
    c: PointOnObject(g6,g-1)
    c: Coincident(g0,g5)
    c: Coincident(g0,g4)
    c: Coincident(g2,g4)
    c: Symmetric(g-3,g7,g3)
FEATURE [PartDesign::Pocket] Pocket001
  BaseFeature = -> Pocket
  Direction = (7e-16,-7e-16,-1)
  Length = 5
  Length2 = 5
  Placement = pos=(0,0,0) rot=(0.57735,0.57735,0.57735;2.0944rad)
  Profile = -> Sketch002
  ReferenceAxis = -> Sketch002 [N_Axis]
  Type = 1
FEATURE [Sketcher::SketchObject] Sketch003
  ExternalGeometry = -> [Pocket001]
  FullyConstrained = true
  MapMode = 5
  Placement = pos=(9.2e-15,21,-1.41e-14) rot=(0.57735,0.57735,0.57735;4.18879rad)
  Support = -> [Pocket001]
  expr: Constraints[0] = <<Datasheet>>#<<mgn9c>>.Dim_d
  expr: Constraints[1] = <<Datasheet>>#<<mgn9c>>.Dim_d
  expr: Constraints[5] = <<Datasheet>>#<<mgn9c>>.Dim_E
  expr: Constraints[6] = <<Datasheet>>#<<mgn9c>>.Dim_P
  sketch-geometry (3):
    g0: Circle CenterX=13.5 CenterY=5.5 CenterZ=0 NormalX=0 NormalY=0 NormalZ=1 AngleXU=0 Radius=1.75
    g1: Circle CenterX=33.5 CenterY=5.5 CenterZ=0 NormalX=0 NormalY=0 NormalZ=1 AngleXU=0 Radius=1.75
    g2: LineSegment StartX=6 StartY=5.5 StartZ=0 EndX=33.5 EndY=5.5 EndZ=0
  constraints (8):
    c: Diameter(g1) = 3.5
    c: Diameter(g0) = 3.5
    c: Coincident(g2,g1)
    c: Horizontal(g2)
    c: PointOnObject(g0,g2)
    c: DistanceX(g2,g0) = 7.5
    c: DistanceX(g0,g1) = 20
    c: Symmetric(g-4,g-4,g2)
FEATURE [PartDesign::Pocket] Pocket002
  BaseFeature = -> Pocket001
  Direction = (-4e-16,-1,6e-16)
  Length = 5
  Length2 = 5
  Placement = pos=(0,0,0) rot=(0.57735,0.57735,0.57735;2.0944rad)
  Profile = -> Sketch003
  ReferenceAxis = -> Sketch003 [N_Axis]
  Type = 1
FEATURE [Sketcher::SketchObject] Sketch005
  ExternalGeometry = -> [Binder]
  FullyConstrained = true
  MapMode = 5
  Placement = pos=(-1e-14,6e-15,6) rot=(0.707107,0.707107,0;3.14159rad)
  sketch-geometry (3):
    g0: Circle CenterX=2.5 CenterY=14.45 CenterZ=0 NormalX=0 NormalY=0 NormalZ=1 AngleXU=0 Radius=1.5
    g1: Circle CenterX=17.5 CenterY=14.45 CenterZ=0 NormalX=0 NormalY=0 NormalZ=1 AngleXU=0 Radius=1.5
    g2: Circle CenterX=2.5 CenterY=4.45 CenterZ=0 NormalX=0 NormalY=0 NormalZ=1 AngleXU=0 Radius=1.5
  constraints (6):
    c: Coincident(g0,g-3)
    c: Tangent(g0,g-3)
    c: Coincident(g1,g-4)
    c: Tangent(g1,g-4)
    c: Coincident(g2,g-5)
    c: Tangent(g2,g-5)
FEATURE [PartDesign::Pocket] Pocket004
  BaseFeature = -> Pocket002
  Direction = (-1.7e-15,1e-15,1)
  Length = 5
  Length2 = 5
  Placement = pos=(0,0,0) rot=(0.57735,0.57735,0.57735;2.0944rad)
  Profile = -> Sketch005
  ReferenceAxis = -> Sketch005 [N_Axis]
  Type = 1
FEATURE [Sketcher::SketchObject] Sketch007
  ExternalGeometry = -> [Pocket004]
  FullyConstrained = true
  MapMode = 5
  Placement = pos=(-8e-16,1.2e-15,2.7564) rot=(0,0,-1;1.5708rad)
  Support = -> [Pocket004]
  expr: .Constraints.Rad = <<OmniballConnector_7945>>#<<Sketch002>>.Constraints.Smallest_Radius
  expr: Constraints[8] = .Constraints.Rad
  sketch-geometry (10):
    g0: LineSegment StartX=12.4944 StartY=18.9 StartZ=0 EndX=2 EndY=18.9 EndZ=0
    g1: LineSegment StartX=2 StartY=18.9 StartZ=0 EndX=2 EndY=5 EndZ=0
    g2: LineSegment StartX=2 StartY=5 StartZ=0 EndX=12.4944 EndY=5 EndZ=0
    g3: LineSegment StartX=12.4944 StartY=5 StartZ=0 EndX=12.4944 EndY=18.9 EndZ=0
    g4: Circle CenterX=8.9958 CenterY=2.5 CenterZ=0 NormalX=0 NormalY=0 NormalZ=1 AngleXU=0 Radius=1.2954
    g5: Circle CenterX=3.9986 CenterY=2.5 CenterZ=0 NormalX=0 NormalY=0 NormalZ=1 AngleXU=0 Radius=1.2954
    g6: GeomPoint X=3.9986 Y=5 Z=0
    g7: GeomPoint X=3.9986 Y=-4e-16 Z=0
    g8: GeomPoint X=7.4972 Y=2.5 Z=0
    g9: GeomPoint X=10.4944 Y=2.5 Z=0
  constraints (21):
    c: Coincident(g0,g1)
    c: Coincident(g1,g2)
    c: Coincident(g2,g3)
    c: Coincident(g3,g0)
    c: Horizontal(g2)
    c: Vertical(g1)
    c: Vertical(g3)
    c: Diameter(g4) = 2.5908  'Rad'
    c: Diameter(g5) = 2.5908
    c: Horizontal(g4,g5)
    c: Coincident(g0,g-5)
    c: PointOnObject(g6,g2)
    c: Symmetric(g6,g7,g5)
    c: Symmetric(g-6,g-7,g7)
    c: Vertical(g5,g7)
    c: DistanceY(g-4,g1) = 5
    c: PointOnObject(g8,g-8)
    c: PointOnObject(g9,g-3)
    c: Symmetric(g9,g8,g4)
    c: Horizontal(g4,g8)
    c: Coincident(g0,g-4)
FEATURE [PartDesign::Pocket] Pocket005
  BaseFeature = -> Pocket004
  Direction = (1.7e-15,-1e-15,-1)
  Length = 5
  Length2 = 5
  Placement = pos=(0,0,0) rot=(0.57735,0.57735,0.57735;2.0944rad)
  Profile = -> Sketch007
  ReferenceAxis = -> Sketch007 [N_Axis]
  Type = 1
FEATURE [PartDesign::SubShapeBinder] Binder002  label="OmniballConnector"
  BindCopyOnChange = 0
  BindMode = 0
  ClaimChildren = false
  Context = -> Body [Binder002.]
  Fuse = false
  MakeFace = true
  OffsetFill = false
  OffsetIntersection = false
  OffsetJoinType = 0
  OffsetOpenResult = false
  PartialLoad = false
  Placement = pos=(2.5,-4,2) rot=(0,1,0;3.14159rad)
  Relative = true
  Support = -> [<external OmniballConnector/OmniballConnector_7945.FCStd>#Body]
  _Version = 2
FEATURE [Sketcher::SketchObject] Sketch008
  ExternalGeometry = -> [Pocket005]
  FullyConstrained = true
  MapMode = 5
  Placement = pos=(-6e-16,9e-16,1.9944) rot=(0,0,-1;1.5708rad)
  Support = -> [Pocket005]
  sketch-geometry (2):
    g0: Circle CenterX=8.9958 CenterY=2.5 CenterZ=0 NormalX=0 NormalY=0 NormalZ=1 AngleXU=0 Radius=1.4986
    g1: Circle CenterX=3.9986 CenterY=2.5 CenterZ=0 NormalX=0 NormalY=0 NormalZ=1 AngleXU=0 Radius=1.4986
  constraints (4):
    c: Coincident(g0,g-3)
    c: Coincident(g1,g-5)
    c: Tangent(g1,g-7)
    c: Tangent(g0,g-4)
FEATURE [PartDesign::SubShapeBinder] Binder003  label="OmniballConnector2"
  BindCopyOnChange = 0
  BindMode = 0
  ClaimChildren = false
  Context = -> Body [Binder003.]
  Fuse = false
  MakeFace = true
  OffsetFill = false
  OffsetIntersection = false
  OffsetJoinType = 0
  OffsetOpenResult = false
  PartialLoad = false
  Placement = pos=(2.5,-9,2) rot=(0,1,0;3.14159rad)
  Relative = true
  Support = -> [<external OmniballConnector/OmniballConnector_7945.FCStd>#Body]
  _Version = 2
FEATURE [PartDesign::Pocket] Pocket006
  BaseFeature = -> Pocket005
  Direction = (3e-16,-4e-16,-1)
  Length = 0.762
  Length2 = 5
  Placement = pos=(0,0,0) rot=(0.57735,0.57735,0.57735;2.0944rad)
  Profile = -> Sketch008
  ReferenceAxis = -> Sketch008 [N_Axis]
  Type = 0
  expr: Length = 0.03 in
FEATURE [PartDesign::Body] Body  label="NormalConnector"
  Group = -> [Binder,Sketch,Binder001,Pad,Sketch001,Pocket,Sketch002,Pocket001,Sketch003,Pocket002,Sketch005,Pocket004,Sketch007,Pocket005,Binder002,Sketch008,Binder003,Pocket006]
  Origin = -> Origin
  Tip = -> Pocket006
---- part parts/PCB_Linear_Potentiometer.FCStd = doc fcstd_4de4bdd4b048 ----
FCSTD DOCUMENT  (FreeCAD 0.21R33668 +26 (Git))
Label: PCB_Linear_Potentiometer
License: All rights reserved
LicenseURL: http://en.wikipedia.org/wiki/All_rights_reserved
objects: Sketcher::SketchObject×3, PartDesign::SubShapeBinder×2, PartDesign::Pad×2, PartDesign::Pocket×1, PartDesign::LinearPattern×1, PartDesign::Body×1
note: 13 computed .brp shape members not serialized (recipe doc carries the construction recipe); baked Part::Feature solids carry a one-line shape summary decoded from their .brp
EXTERNAL_REF file=MG/mgn9c_13.FCStd obj=Body
EXTERNAL_REF file=MG/mgn9c_slide.FCStd obj=Body001
EXTERNAL_REF file=MG/Datasheet.FCStd obj=Spreadsheet
EXTERNAL_REF file=NormalConnector.FCStd obj=Sketch
EXTERNAL_REF file=Base.FCStd obj=Sketch001
EXTERNAL_REF file=Base.FCStd obj=Sketch

FEATURE [PartDesign::SubShapeBinder] Binder  label="Rail"
  BindCopyOnChange = 0
  BindMode = 0
  ClaimChildren = false
  Context = -> Body [Binder.]
  Fuse = false
  MakeFace = true
  OffsetFill = false
  OffsetIntersection = false
  OffsetJoinType = 0
  OffsetOpenResult = false
  PartialLoad = false
  Relative = true
  Support = -> [<external MG/mgn9c_13.FCStd>#Body]
  _Version = 2
FEATURE [PartDesign::SubShapeBinder] Binder001  label="Slide"
  BindCopyOnChange = 0
  BindMode = 0
  ClaimChildren = false
  Context = -> Body [Binder001.]
  Fuse = false
  MakeFace = true
  OffsetFill = false
  OffsetIntersection = false
  OffsetJoinType = 0
  OffsetOpenResult = false
  PartialLoad = false
  Placement = pos=(0,-5.5,0) rot=(0,0,1;0rad)
  Relative = true
  Support = -> [<external MG/mgn9c_slide.FCStd>#Body001]
  _Version = 2
FEATURE [Sketcher::SketchObject] Sketch
  ExternalGeometry = -> [Binder]
  FullyConstrained = true
  MapMode = 5
  Support = -> [XY_Plane]
  expr: Constraints[21] = <<Datasheet>>#<<mgn9c>>.Dim_W
  expr: Constraints[22] = NormalConnector#Sketch.Constraints.PCB_Edge_Distance_From_Slide_Side
  sketch-geometry (11):
    g0: LineSegment StartX=0 StartY=9 StartZ=0 EndX=255 EndY=9 EndZ=0
    g1: LineSegment StartX=255 StartY=9 StartZ=0 EndX=255 EndY=-17.9944 EndZ=0
    g2: LineSegment StartX=255 StartY=-17.9944 StartZ=0 EndX=0 EndY=-17.9944 EndZ=0
    g3: LineSegment StartX=0 StartY=-17.9944 StartZ=0 EndX=0 EndY=9 EndZ=0
    g4: LineSegment StartX=7.5 StartY=4.5 StartZ=0 EndX=27.5 EndY=4.5 EndZ=0
    g5: LineSegment StartX=7.5 StartY=14.5 StartZ=0 EndX=27.5 EndY=14.5 EndZ=0
    g6: LineSegment StartX=27.5 StartY=14.5 StartZ=0 EndX=27.5 EndY=-5.5 EndZ=0
    g7: LineSegment StartX=27.5 StartY=-5.5 StartZ=0 EndX=7.5 EndY=-5.5 EndZ=0
    g8: LineSegment StartX=7.5 StartY=-5.5 StartZ=0 EndX=7.5 EndY=14.5 EndZ=0
    g9: Circle CenterX=7.5 CenterY=4.5 CenterZ=0 NormalX=0 NormalY=0 NormalZ=1 AngleXU=0 Radius=1.75
    g10: GeomPoint X=9.25 Y=4.5 Z=0
  constraints (29):
    c: Coincident(g0,g1)
    c: Coincident(g1,g2)
    c: Coincident(g2,g3)
    c: Coincident(g3,g0)
    c: Horizontal(g2)
    c: Vertical(g1)
    c: Vertical(g3)
    c: Coincident(g0,g-3)
    c: Coincident(g0,g-4)
    c: Coincident(g4,g-5)
    c: Coincident(g4,g-6)
    c: Coincident(g5,g6)
    c: Coincident(g6,g7)
    c: Coincident(g7,g8)
    c: Coincident(g8,g5)
    c: Horizontal(g5)
    c: Horizontal(g7)
    c: Vertical(g6)
    c: PointOnObject(g4,g6)
    c: PointOnObject(g4,g8)
    c: Symmetric(g5,g7,g4)
    c: DistanceY(g8,g8) = 20
    c: DistanceY(g2,g7) = 12.4944
    c: Coincident(g9,g4)
    c: PointOnObject(g10,g4)
    c: PointOnObject(g10,g-5)
    c: PointOnObject(g10,g9)
    c: DistanceX(g0,g0) = 255  'Length'
    c: DistanceY(g1,g1) = 26.9944
FEATURE [PartDesign::Pad] Pad
  Direction = (0,0,1)
  Length = 2
  Length2 = 10
  Profile = -> Sketch
  ReferenceAxis = -> Sketch [N_Axis]
  Type = 0
  expr: Length = <<Base>>#<<Sketch001>>.Constraints.PCB_Thickness
FEATURE [Sketcher::SketchObject] Sketch001
  ExternalGeometry = -> [Pad]
  FullyConstrained = true
  MapMode = 5
  Placement = pos=(0,0,2) rot=(0,0,1;0rad)
  Support = -> [Pad]
  sketch-geometry (2):
    g0: Circle CenterX=7.5 CenterY=4.5 CenterZ=0 NormalX=0 NormalY=0 NormalZ=1 AngleXU=0 Radius=1.75
    g1: GeomPoint X=9.25 Y=4.5 Z=0
  constraints (4):
    c: PointOnObject(g1,g0)
    c: PointOnObject(g1,g-3)
    c: Coincident(g0,g-3)
    c: DistanceY(g1,g0) = 0
FEATURE [PartDesign::Pocket] Pocket
  BaseFeature = -> Pad
  Direction = (0,0,-1)
  Length = 5
  Length2 = 5
  Profile = -> Sketch001
  ReferenceAxis = -> Sketch001 [N_Axis]
  Type = 1
FEATURE [PartDesign::LinearPattern] LinearPattern
  BaseFeature = -> Pocket
  Direction = -> Sketch001 [H_Axis]
  Length = 240
  Occurrences = 13
  Originals = -> [Pocket]
  expr: Length = <<Sketch>>.Constraints.Length - <<Datasheet>>#<<mgn9c>>.Dim_E * 2
FEATURE [Sketcher::SketchObject] Sketch002
  ExternalGeometry = -> [LinearPattern]
  FullyConstrained = true
  MapMode = 5
  Placement = pos=(0,0,2) rot=(0,0,1;0rad)
  Support = -> [LinearPattern]
  expr: Constraints[18] = <<Datasheet>>#<<mgn9c>>.Dim_W / 2
  expr: Constraints[21] = NormalConnector#Sketch.Constraints.Connector_Close_Distance
  expr: Constraints[22] = NormalConnector#Sketch.Constraints.Connector_Far_Distance
  expr: Constraints[24] = .Constraints.Resistor_Width
  expr: Constraints[26] = <<Base>>#<<Sketch>>.Constraints.RailOverlap
  sketch-geometry (15):
    g0: LineSegment StartX=12.25 StartY=-7.4986 StartZ=0 EndX=242.75 EndY=-7.4986 EndZ=0
    g1: LineSegment StartX=242.75 StartY=-7.4986 StartZ=0 EndX=242.75 EndY=-11.4986 EndZ=0
    g2: LineSegment StartX=242.75 StartY=-11.4986 StartZ=0 EndX=12.25 EndY=-11.4986 EndZ=0
    g3: LineSegment StartX=12.25 StartY=-11.4986 StartZ=0 EndX=12.25 EndY=-7.4986 EndZ=0
    g4: LineSegment StartX=12.25 StartY=-12.4958 StartZ=0 EndX=242.75 EndY=-12.4958 EndZ=0
    g5: LineSegment StartX=242.75 StartY=-12.4958 StartZ=0 EndX=242.75 EndY=-16.4958 EndZ=0
    g6: LineSegment StartX=242.75 StartY=-16.4958 StartZ=0 EndX=12.25 EndY=-16.4958 EndZ=0
    g7: LineSegment StartX=12.25 StartY=-16.4958 StartZ=0 EndX=12.25 EndY=-12.4958 EndZ=0
    g8: GeomPoint X=12.25 Y=-9.4986 Z=0
    g9: GeomPoint X=12.25 Y=-14.4958 Z=0
    g10: GeomPoint X=0 Y=4.5 Z=0
    g11: GeomPoint X=0 Y=-5.5 Z=0
    g12: GeomPoint X=12.25 Y=9 Z=0
    g13: GeomPoint X=242.75 Y=9 Z=0
    g14: GeomPoint X=127.5 Y=9 Z=0
  constraints (33):
    c: Coincident(g0,g1)
    c: Coincident(g1,g2)
    c: Coincident(g2,g3)
    c: Coincident(g3,g0)
    c: Horizontal(g0)
    c: Horizontal(g2)
    c: Vertical(g1)
    c: Vertical(g3)
    c: Coincident(g4,g5)
    c: Coincident(g5,g6)
    c: Coincident(g6,g7)
    c: Coincident(g7,g4)
    c: Horizontal(g4)
    c: Horizontal(g6)
    c: Vertical(g5)
    c: Vertical(g7)
    c: Symmetric(g-4,g-1,g10)
    c: PointOnObject(g11,g-4)
    c: DistanceY(g11,g10) = 10
    c: Symmetric(g2,g0,g8)
    c: Symmetric(g4,g6,g9)
    c: DistanceY(g8,g11) = 3.9986
    c: DistanceY(g9,g11) = 8.9958
    c: DistanceY(g3,g3) = 4  'Resistor_Width'
    c: DistanceY(g7,g7) = 4
    c: PointOnObject(g12,g-7)
    c: DistanceX(g-7,g12) = 12.25
    c: Vertical(g8,g9)
    c: Vertical(g12,g8)
    c: Symmetric(g13,g12,g14)
    c: Symmetric(g-7,g-7,g14)
    c: Vertical(g0,g13)
    c: Vertical(g4,g1)
FEATURE [PartDesign::Pad] Pad001
  BaseFeature = -> LinearPattern
  Direction = (0,0,1)
  Length = 0.1
  Length2 = 10
  Profile = -> Sketch002
  ReferenceAxis = -> Sketch002 [N_Axis]
  Type = 0
FEATURE [PartDesign::Body] Body  label="PCB"
  Group = -> [Binder,Binder001,Sketch,Pad,Sketch001,Pocket,LinearPattern,Sketch002,Pad001]
  Origin = -> Origin
  Tip = -> Pad001
